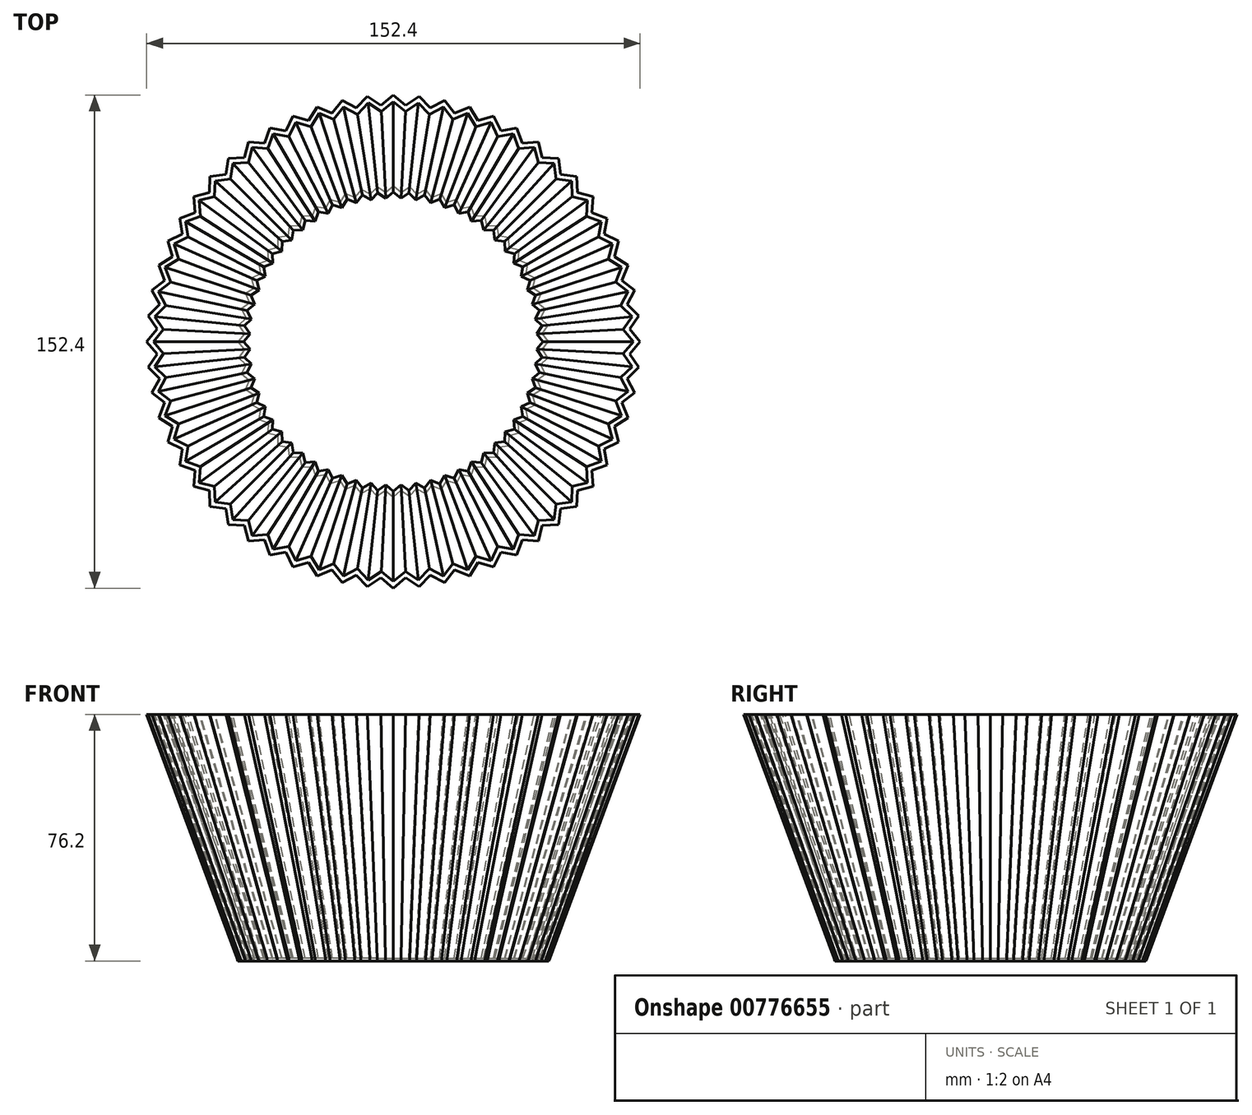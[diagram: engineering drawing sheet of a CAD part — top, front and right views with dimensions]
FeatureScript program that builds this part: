
annotation { "Feature Type Name" : "Feature", "Feature Type Description" : "" }
export const myFeature = defineFeature(function(context is Context, id is Id, definition is map)
    precondition{}
    {
        {
            var Q0;
            Q0=qCreatedBy(makeId("Top.planeOp"),FACE);
            var sketch = newSketch(context, id + "F0", { "sketchPlane" : qUnion([Q0])});
            skLineSegment(sketch, "E0", {"start": v(0, 0) * mm, "end": v(3.83, 73) * mm, "construction": true});
            skLineSegment(sketch, "E1", {"start": v(3.83, 73) * mm, "end": v(0, 73) * mm, "construction": true});
            skLineSegment(sketch, "E2", {"start": v(0, 73) * mm, "end": v(0, 0) * mm, "construction": true});
            skLineSegment(sketch, "E3", {"start": v(3.83, 73) * mm, "end": v(0, 76.2) * mm});
            skLineSegment(sketch, "E4.MirrorCS", {"start": v(-3.83, 73) * mm, "end": v(0, 76.2) * mm});
            skLineSegment(sketch, "E5.1.0", {"start": v(-11.43, 72.2) * mm, "end": v(-7.97, 75.78) * mm});
            skLineSegment(sketch, "E5.1.1", {"start": v(-3.83, 73) * mm, "end": v(-7.97, 75.78) * mm});
            skLineSegment(sketch, "E5.2.0", {"start": v(-18.92, 70.6) * mm, "end": v(-15.84, 74.53) * mm});
            skLineSegment(sketch, "E5.2.1", {"start": v(-11.43, 72.2) * mm, "end": v(-15.84, 74.53) * mm});
            skLineSegment(sketch, "E5.3.0", {"start": v(-26.2, 68.24) * mm, "end": v(-23.55, 72.47) * mm});
            skLineSegment(sketch, "E5.3.1", {"start": v(-18.92, 70.6) * mm, "end": v(-23.55, 72.47) * mm});
            skLineSegment(sketch, "E5.4.0", {"start": v(-33.18, 65.12) * mm, "end": v(-31, 69.61) * mm});
            skLineSegment(sketch, "E5.4.1", {"start": v(-26.2, 68.24) * mm, "end": v(-31, 69.61) * mm});
            skLineSegment(sketch, "E5.5.0", {"start": v(-39.8, 61.3) * mm, "end": v(-38.1, 66) * mm});
            skLineSegment(sketch, "E5.5.1", {"start": v(-33.18, 65.12) * mm, "end": v(-38.1, 66) * mm});
            skLineSegment(sketch, "E5.6.0", {"start": v(-46, 56.8) * mm, "end": v(-44.79, 61.65) * mm});
            skLineSegment(sketch, "E5.6.1", {"start": v(-39.8, 61.3) * mm, "end": v(-44.79, 61.65) * mm});
            skLineSegment(sketch, "E5.7.0", {"start": v(-51.68, 51.68) * mm, "end": v(-50.99, 56.63) * mm});
            skLineSegment(sketch, "E5.7.1", {"start": v(-46, 56.8) * mm, "end": v(-50.99, 56.63) * mm});
            skLineSegment(sketch, "E5.8.0", {"start": v(-56.8, 46) * mm, "end": v(-56.63, 50.99) * mm});
            skLineSegment(sketch, "E5.8.1", {"start": v(-51.68, 51.68) * mm, "end": v(-56.63, 50.99) * mm});
            skLineSegment(sketch, "E5.9.0", {"start": v(-61.3, 39.8) * mm, "end": v(-61.65, 44.79) * mm});
            skLineSegment(sketch, "E5.9.1", {"start": v(-56.8, 46) * mm, "end": v(-61.65, 44.79) * mm});
            skLineSegment(sketch, "E5.10.0", {"start": v(-65.12, 33.18) * mm, "end": v(-66, 38.1) * mm});
            skLineSegment(sketch, "E5.10.1", {"start": v(-61.3, 39.8) * mm, "end": v(-66, 38.1) * mm});
            skLineSegment(sketch, "E5.11.0", {"start": v(-68.24, 26.2) * mm, "end": v(-69.61, 31) * mm});
            skLineSegment(sketch, "E5.11.1", {"start": v(-65.12, 33.18) * mm, "end": v(-69.61, 31) * mm});
            skLineSegment(sketch, "E5.12.0", {"start": v(-70.6, 18.92) * mm, "end": v(-72.47, 23.55) * mm});
            skLineSegment(sketch, "E5.12.1", {"start": v(-68.24, 26.2) * mm, "end": v(-72.47, 23.55) * mm});
            skLineSegment(sketch, "E5.13.0", {"start": v(-72.2, 11.43) * mm, "end": v(-74.53, 15.84) * mm});
            skLineSegment(sketch, "E5.13.1", {"start": v(-70.6, 18.92) * mm, "end": v(-74.53, 15.84) * mm});
            skLineSegment(sketch, "E5.14.0", {"start": v(-73, 3.83) * mm, "end": v(-75.78, 7.97) * mm});
            skLineSegment(sketch, "E5.14.1", {"start": v(-72.2, 11.43) * mm, "end": v(-75.78, 7.97) * mm});
            skLineSegment(sketch, "E5.15.0", {"start": v(-73, -3.83) * mm, "end": v(-76.2, 0) * mm});
            skLineSegment(sketch, "E5.15.1", {"start": v(-73, 3.83) * mm, "end": v(-76.2, 0) * mm});
            skLineSegment(sketch, "E5.16.0", {"start": v(-72.2, -11.43) * mm, "end": v(-75.78, -7.97) * mm});
            skLineSegment(sketch, "E5.16.1", {"start": v(-73, -3.83) * mm, "end": v(-75.78, -7.97) * mm});
            skLineSegment(sketch, "E5.17.0", {"start": v(-70.6, -18.92) * mm, "end": v(-74.53, -15.84) * mm});
            skLineSegment(sketch, "E5.17.1", {"start": v(-72.2, -11.43) * mm, "end": v(-74.53, -15.84) * mm});
            skLineSegment(sketch, "E5.18.0", {"start": v(-68.24, -26.2) * mm, "end": v(-72.47, -23.55) * mm});
            skLineSegment(sketch, "E5.18.1", {"start": v(-70.6, -18.92) * mm, "end": v(-72.47, -23.55) * mm});
            skLineSegment(sketch, "E5.19.0", {"start": v(-65.12, -33.18) * mm, "end": v(-69.61, -31) * mm});
            skLineSegment(sketch, "E5.19.1", {"start": v(-68.24, -26.2) * mm, "end": v(-69.61, -31) * mm});
            skLineSegment(sketch, "E5.20.0", {"start": v(-61.3, -39.8) * mm, "end": v(-66, -38.1) * mm});
            skLineSegment(sketch, "E5.20.1", {"start": v(-65.12, -33.18) * mm, "end": v(-66, -38.1) * mm});
            skLineSegment(sketch, "E5.21.0", {"start": v(-56.8, -46) * mm, "end": v(-61.65, -44.79) * mm});
            skLineSegment(sketch, "E5.21.1", {"start": v(-61.3, -39.8) * mm, "end": v(-61.65, -44.79) * mm});
            skLineSegment(sketch, "E5.22.0", {"start": v(-51.68, -51.68) * mm, "end": v(-56.63, -50.99) * mm});
            skLineSegment(sketch, "E5.22.1", {"start": v(-56.8, -46) * mm, "end": v(-56.63, -50.99) * mm});
            skLineSegment(sketch, "E5.23.0", {"start": v(-46, -56.8) * mm, "end": v(-50.99, -56.63) * mm});
            skLineSegment(sketch, "E5.23.1", {"start": v(-51.68, -51.68) * mm, "end": v(-50.99, -56.63) * mm});
            skLineSegment(sketch, "E5.24.0", {"start": v(-39.8, -61.3) * mm, "end": v(-44.79, -61.65) * mm});
            skLineSegment(sketch, "E5.24.1", {"start": v(-46, -56.8) * mm, "end": v(-44.79, -61.65) * mm});
            skLineSegment(sketch, "E5.25.0", {"start": v(-33.18, -65.12) * mm, "end": v(-38.1, -66) * mm});
            skLineSegment(sketch, "E5.25.1", {"start": v(-39.8, -61.3) * mm, "end": v(-38.1, -66) * mm});
            skLineSegment(sketch, "E5.26.0", {"start": v(-26.2, -68.24) * mm, "end": v(-31, -69.61) * mm});
            skLineSegment(sketch, "E5.26.1", {"start": v(-33.18, -65.12) * mm, "end": v(-31, -69.61) * mm});
            skLineSegment(sketch, "E5.27.0", {"start": v(-18.92, -70.6) * mm, "end": v(-23.55, -72.47) * mm});
            skLineSegment(sketch, "E5.27.1", {"start": v(-26.2, -68.24) * mm, "end": v(-23.55, -72.47) * mm});
            skLineSegment(sketch, "E5.28.0", {"start": v(-11.43, -72.2) * mm, "end": v(-15.84, -74.53) * mm});
            skLineSegment(sketch, "E5.28.1", {"start": v(-18.92, -70.6) * mm, "end": v(-15.84, -74.53) * mm});
            skLineSegment(sketch, "E5.29.0", {"start": v(-3.83, -73) * mm, "end": v(-7.97, -75.78) * mm});
            skLineSegment(sketch, "E5.29.1", {"start": v(-11.43, -72.2) * mm, "end": v(-7.97, -75.78) * mm});
            skLineSegment(sketch, "E5.30.0", {"start": v(3.83, -73) * mm, "end": v(0, -76.2) * mm});
            skLineSegment(sketch, "E5.30.1", {"start": v(-3.83, -73) * mm, "end": v(0, -76.2) * mm});
            skLineSegment(sketch, "E5.31.0", {"start": v(11.43, -72.2) * mm, "end": v(7.97, -75.78) * mm});
            skLineSegment(sketch, "E5.31.1", {"start": v(3.83, -73) * mm, "end": v(7.97, -75.78) * mm});
            skLineSegment(sketch, "E5.32.0", {"start": v(18.92, -70.6) * mm, "end": v(15.84, -74.53) * mm});
            skLineSegment(sketch, "E5.32.1", {"start": v(11.43, -72.2) * mm, "end": v(15.84, -74.53) * mm});
            skLineSegment(sketch, "E5.33.0", {"start": v(26.2, -68.24) * mm, "end": v(23.55, -72.47) * mm});
            skLineSegment(sketch, "E5.33.1", {"start": v(18.92, -70.6) * mm, "end": v(23.55, -72.47) * mm});
            skLineSegment(sketch, "E5.34.0", {"start": v(33.18, -65.12) * mm, "end": v(31, -69.61) * mm});
            skLineSegment(sketch, "E5.34.1", {"start": v(26.2, -68.24) * mm, "end": v(31, -69.61) * mm});
            skLineSegment(sketch, "E5.35.0", {"start": v(39.8, -61.3) * mm, "end": v(38.1, -66) * mm});
            skLineSegment(sketch, "E5.35.1", {"start": v(33.18, -65.12) * mm, "end": v(38.1, -66) * mm});
            skLineSegment(sketch, "E5.36.0", {"start": v(46, -56.8) * mm, "end": v(44.79, -61.65) * mm});
            skLineSegment(sketch, "E5.36.1", {"start": v(39.8, -61.3) * mm, "end": v(44.79, -61.65) * mm});
            skLineSegment(sketch, "E5.37.0", {"start": v(51.68, -51.68) * mm, "end": v(50.99, -56.63) * mm});
            skLineSegment(sketch, "E5.37.1", {"start": v(46, -56.8) * mm, "end": v(50.99, -56.63) * mm});
            skLineSegment(sketch, "E5.38.0", {"start": v(56.8, -46) * mm, "end": v(56.63, -50.99) * mm});
            skLineSegment(sketch, "E5.38.1", {"start": v(51.68, -51.68) * mm, "end": v(56.63, -50.99) * mm});
            skLineSegment(sketch, "E5.39.0", {"start": v(61.3, -39.8) * mm, "end": v(61.65, -44.79) * mm});
            skLineSegment(sketch, "E5.39.1", {"start": v(56.8, -46) * mm, "end": v(61.65, -44.79) * mm});
            skLineSegment(sketch, "E5.40.0", {"start": v(65.12, -33.18) * mm, "end": v(66, -38.1) * mm});
            skLineSegment(sketch, "E5.40.1", {"start": v(61.3, -39.8) * mm, "end": v(66, -38.1) * mm});
            skLineSegment(sketch, "E5.41.0", {"start": v(68.24, -26.2) * mm, "end": v(69.61, -31) * mm});
            skLineSegment(sketch, "E5.41.1", {"start": v(65.12, -33.18) * mm, "end": v(69.61, -31) * mm});
            skLineSegment(sketch, "E5.42.0", {"start": v(70.6, -18.92) * mm, "end": v(72.47, -23.55) * mm});
            skLineSegment(sketch, "E5.42.1", {"start": v(68.24, -26.2) * mm, "end": v(72.47, -23.55) * mm});
            skLineSegment(sketch, "E5.43.0", {"start": v(72.2, -11.43) * mm, "end": v(74.53, -15.84) * mm});
            skLineSegment(sketch, "E5.43.1", {"start": v(70.6, -18.92) * mm, "end": v(74.53, -15.84) * mm});
            skLineSegment(sketch, "E5.44.0", {"start": v(73, -3.83) * mm, "end": v(75.78, -7.97) * mm});
            skLineSegment(sketch, "E5.44.1", {"start": v(72.2, -11.43) * mm, "end": v(75.78, -7.97) * mm});
            skLineSegment(sketch, "E5.45.0", {"start": v(73, 3.83) * mm, "end": v(76.2, 0) * mm});
            skLineSegment(sketch, "E5.45.1", {"start": v(73, -3.83) * mm, "end": v(76.2, 0) * mm});
            skLineSegment(sketch, "E5.46.0", {"start": v(72.2, 11.43) * mm, "end": v(75.78, 7.97) * mm});
            skLineSegment(sketch, "E5.46.1", {"start": v(73, 3.83) * mm, "end": v(75.78, 7.97) * mm});
            skLineSegment(sketch, "E5.47.0", {"start": v(70.6, 18.92) * mm, "end": v(74.53, 15.84) * mm});
            skLineSegment(sketch, "E5.47.1", {"start": v(72.2, 11.43) * mm, "end": v(74.53, 15.84) * mm});
            skLineSegment(sketch, "E5.48.0", {"start": v(68.24, 26.2) * mm, "end": v(72.47, 23.55) * mm});
            skLineSegment(sketch, "E5.48.1", {"start": v(70.6, 18.92) * mm, "end": v(72.47, 23.55) * mm});
            skLineSegment(sketch, "E5.49.0", {"start": v(65.12, 33.18) * mm, "end": v(69.61, 31) * mm});
            skLineSegment(sketch, "E5.49.1", {"start": v(68.24, 26.2) * mm, "end": v(69.61, 31) * mm});
            skLineSegment(sketch, "E5.50.0", {"start": v(61.3, 39.8) * mm, "end": v(66, 38.1) * mm});
            skLineSegment(sketch, "E5.50.1", {"start": v(65.12, 33.18) * mm, "end": v(66, 38.1) * mm});
            skLineSegment(sketch, "E5.51.0", {"start": v(56.8, 46) * mm, "end": v(61.65, 44.79) * mm});
            skLineSegment(sketch, "E5.51.1", {"start": v(61.3, 39.8) * mm, "end": v(61.65, 44.79) * mm});
            skLineSegment(sketch, "E5.52.0", {"start": v(51.68, 51.68) * mm, "end": v(56.63, 50.99) * mm});
            skLineSegment(sketch, "E5.52.1", {"start": v(56.8, 46) * mm, "end": v(56.63, 50.99) * mm});
            skLineSegment(sketch, "E5.53.0", {"start": v(46, 56.8) * mm, "end": v(50.99, 56.63) * mm});
            skLineSegment(sketch, "E5.53.1", {"start": v(51.68, 51.68) * mm, "end": v(50.99, 56.63) * mm});
            skLineSegment(sketch, "E5.54.0", {"start": v(39.8, 61.3) * mm, "end": v(44.79, 61.65) * mm});
            skLineSegment(sketch, "E5.54.1", {"start": v(46, 56.8) * mm, "end": v(44.79, 61.65) * mm});
            skLineSegment(sketch, "E5.55.0", {"start": v(33.18, 65.12) * mm, "end": v(38.1, 66) * mm});
            skLineSegment(sketch, "E5.55.1", {"start": v(39.8, 61.3) * mm, "end": v(38.1, 66) * mm});
            skLineSegment(sketch, "E5.56.0", {"start": v(26.2, 68.24) * mm, "end": v(31, 69.61) * mm});
            skLineSegment(sketch, "E5.56.1", {"start": v(33.18, 65.12) * mm, "end": v(31, 69.61) * mm});
            skLineSegment(sketch, "E5.57.0", {"start": v(18.92, 70.6) * mm, "end": v(23.55, 72.47) * mm});
            skLineSegment(sketch, "E5.57.1", {"start": v(26.2, 68.24) * mm, "end": v(23.55, 72.47) * mm});
            skLineSegment(sketch, "E5.58.0", {"start": v(11.43, 72.2) * mm, "end": v(15.84, 74.53) * mm});
            skLineSegment(sketch, "E5.58.1", {"start": v(18.92, 70.6) * mm, "end": v(15.84, 74.53) * mm});
            skLineSegment(sketch, "E5.59.0", {"start": v(3.83, 73) * mm, "end": v(7.97, 75.78) * mm});
            skLineSegment(sketch, "E5.59.1", {"start": v(11.43, 72.2) * mm, "end": v(7.97, 75.78) * mm});
            skPoint(sketch, "E5.center", {"position": v(0, 0) * mm});
            skLineSegment(sketch, "E6.0", {"start": v(-68.68, 18.4) * mm, "end": v(-70.5, 22.9) * mm});
            skLineSegment(sketch, "E6.1", {"start": v(-66.38, 25.48) * mm, "end": v(-70.5, 22.9) * mm});
            skLineSegment(sketch, "E6.2", {"start": v(-66.38, 25.48) * mm, "end": v(-67.72, 30.15) * mm});
            skLineSegment(sketch, "E6.3", {"start": v(-63.35, 32.28) * mm, "end": v(-67.72, 30.15) * mm});
            skLineSegment(sketch, "E6.4", {"start": v(-63.35, 32.28) * mm, "end": v(-64.2, 37.06) * mm});
            skLineSegment(sketch, "E6.5", {"start": v(-59.63, 38.73) * mm, "end": v(-64.2, 37.06) * mm});
            skLineSegment(sketch, "E6.6", {"start": v(-59.63, 38.73) * mm, "end": v(-59.97, 43.57) * mm});
            skLineSegment(sketch, "E6.7", {"start": v(-55.26, 44.75) * mm, "end": v(-59.97, 43.57) * mm});
            skLineSegment(sketch, "E6.8", {"start": v(-55.26, 44.75) * mm, "end": v(-55.09, 49.6) * mm});
            skLineSegment(sketch, "E6.9", {"start": v(-50.28, 50.28) * mm, "end": v(-55.09, 49.6) * mm});
            skLineSegment(sketch, "E6.10", {"start": v(-50.28, 50.28) * mm, "end": v(-49.6, 55.09) * mm});
            skLineSegment(sketch, "E6.11", {"start": v(-44.75, 55.26) * mm, "end": v(-49.6, 55.09) * mm});
            skLineSegment(sketch, "E6.12", {"start": v(-44.75, 55.26) * mm, "end": v(-43.57, 59.97) * mm});
            skLineSegment(sketch, "E6.13", {"start": v(-38.73, 59.63) * mm, "end": v(-43.57, 59.97) * mm});
            skLineSegment(sketch, "E6.14", {"start": v(-38.73, 59.63) * mm, "end": v(-37.06, 64.2) * mm});
            skLineSegment(sketch, "E6.15", {"start": v(-32.28, 63.35) * mm, "end": v(-37.06, 64.2) * mm});
            skLineSegment(sketch, "E6.16", {"start": v(-32.28, 63.35) * mm, "end": v(-30.15, 67.72) * mm});
            skLineSegment(sketch, "E6.17", {"start": v(-25.48, 66.38) * mm, "end": v(-30.15, 67.72) * mm});
            skLineSegment(sketch, "E6.18", {"start": v(-25.48, 66.38) * mm, "end": v(-22.9, 70.5) * mm});
            skLineSegment(sketch, "E6.19", {"start": v(-18.4, 68.68) * mm, "end": v(-22.9, 70.5) * mm});
            skLineSegment(sketch, "E6.20", {"start": v(-18.4, 68.68) * mm, "end": v(-15.41, 72.5) * mm});
            skLineSegment(sketch, "E6.21", {"start": v(-11.12, 70.23) * mm, "end": v(-15.41, 72.5) * mm});
            skLineSegment(sketch, "E6.22", {"start": v(-11.12, 70.23) * mm, "end": v(-7.75, 73.72) * mm});
            skLineSegment(sketch, "E6.23", {"start": v(38.73, -59.63) * mm, "end": v(43.57, -59.97) * mm});
            skLineSegment(sketch, "E6.24", {"start": v(38.73, -59.63) * mm, "end": v(37.06, -64.2) * mm});
            skLineSegment(sketch, "E6.25", {"start": v(32.28, -63.35) * mm, "end": v(37.06, -64.2) * mm});
            skLineSegment(sketch, "E6.26", {"start": v(32.28, -63.35) * mm, "end": v(30.15, -67.72) * mm});
            skLineSegment(sketch, "E6.27", {"start": v(25.48, -66.38) * mm, "end": v(30.15, -67.72) * mm});
            skLineSegment(sketch, "E6.28", {"start": v(25.48, -66.38) * mm, "end": v(22.9, -70.5) * mm});
            skLineSegment(sketch, "E6.29", {"start": v(18.4, -68.68) * mm, "end": v(22.9, -70.5) * mm});
            skLineSegment(sketch, "E6.30", {"start": v(18.4, -68.68) * mm, "end": v(15.41, -72.5) * mm});
            skLineSegment(sketch, "E6.31", {"start": v(11.12, -70.23) * mm, "end": v(15.41, -72.5) * mm});
            skLineSegment(sketch, "E6.32", {"start": v(11.12, -70.23) * mm, "end": v(7.75, -73.72) * mm});
            skLineSegment(sketch, "E6.33", {"start": v(3.72, -71) * mm, "end": v(7.75, -73.72) * mm});
            skLineSegment(sketch, "E6.34", {"start": v(3.72, -71) * mm, "end": v(0, -74.13) * mm});
            skLineSegment(sketch, "E6.35", {"start": v(-3.72, -71) * mm, "end": v(0, -74.13) * mm});
            skLineSegment(sketch, "E6.36", {"start": v(-3.72, -71) * mm, "end": v(-7.75, -73.72) * mm});
            skLineSegment(sketch, "E6.37", {"start": v(-11.12, -70.23) * mm, "end": v(-7.75, -73.72) * mm});
            skLineSegment(sketch, "E6.38", {"start": v(-11.12, -70.23) * mm, "end": v(-15.41, -72.5) * mm});
            skLineSegment(sketch, "E6.39", {"start": v(-18.4, -68.68) * mm, "end": v(-15.41, -72.5) * mm});
            skLineSegment(sketch, "E6.40", {"start": v(-18.4, -68.68) * mm, "end": v(-22.9, -70.5) * mm});
            skLineSegment(sketch, "E6.41", {"start": v(-25.48, -66.38) * mm, "end": v(-22.9, -70.5) * mm});
            skLineSegment(sketch, "E6.42", {"start": v(-25.48, -66.38) * mm, "end": v(-30.15, -67.72) * mm});
            skLineSegment(sketch, "E6.43", {"start": v(-32.28, -63.35) * mm, "end": v(-30.15, -67.72) * mm});
            skLineSegment(sketch, "E6.44", {"start": v(-32.28, -63.35) * mm, "end": v(-37.06, -64.2) * mm});
            skLineSegment(sketch, "E6.45", {"start": v(-38.73, -59.63) * mm, "end": v(-37.06, -64.2) * mm});
            skLineSegment(sketch, "E6.46", {"start": v(-38.73, -59.63) * mm, "end": v(-43.57, -59.97) * mm});
            skLineSegment(sketch, "E6.47", {"start": v(-68.68, -18.4) * mm, "end": v(-70.5, -22.9) * mm});
            skLineSegment(sketch, "E6.48", {"start": v(-68.68, -18.4) * mm, "end": v(-72.5, -15.41) * mm});
            skLineSegment(sketch, "E6.49", {"start": v(-70.23, -11.12) * mm, "end": v(-72.5, -15.41) * mm});
            skLineSegment(sketch, "E6.50", {"start": v(-70.23, -11.12) * mm, "end": v(-73.72, -7.75) * mm});
            skLineSegment(sketch, "E6.51", {"start": v(-71, -3.72) * mm, "end": v(-73.72, -7.75) * mm});
            skLineSegment(sketch, "E6.52", {"start": v(-71, -3.72) * mm, "end": v(-74.13, 0) * mm});
            skLineSegment(sketch, "E6.53", {"start": v(-70.23, 11.12) * mm, "end": v(-72.5, 15.41) * mm});
            skLineSegment(sketch, "E6.54", {"start": v(-70.23, 11.12) * mm, "end": v(-73.72, 7.75) * mm});
            skLineSegment(sketch, "E6.55", {"start": v(-71, 3.72) * mm, "end": v(-73.72, 7.75) * mm});
            skLineSegment(sketch, "E6.56", {"start": v(-71, 3.72) * mm, "end": v(-74.13, 0) * mm});
            skLineSegment(sketch, "E6.57", {"start": v(-66.38, -25.48) * mm, "end": v(-70.5, -22.9) * mm});
            skLineSegment(sketch, "E6.58", {"start": v(-66.38, -25.48) * mm, "end": v(-67.72, -30.15) * mm});
            skLineSegment(sketch, "E6.59", {"start": v(-63.35, -32.28) * mm, "end": v(-67.72, -30.15) * mm});
            skLineSegment(sketch, "E6.60", {"start": v(-63.35, -32.28) * mm, "end": v(-64.2, -37.06) * mm});
            skLineSegment(sketch, "E6.63", {"start": v(-55.26, -44.75) * mm, "end": v(-59.97, -43.57) * mm});
            skLineSegment(sketch, "E6.64", {"start": v(-55.26, -44.75) * mm, "end": v(-55.09, -49.6) * mm});
            skLineSegment(sketch, "E6.65", {"start": v(-50.28, -50.28) * mm, "end": v(-55.09, -49.6) * mm});
            skLineSegment(sketch, "E6.66", {"start": v(-50.28, -50.28) * mm, "end": v(-49.6, -55.09) * mm});
            skLineSegment(sketch, "E6.67", {"start": v(-44.75, -55.26) * mm, "end": v(-49.6, -55.09) * mm});
            skLineSegment(sketch, "E6.68", {"start": v(-44.75, -55.26) * mm, "end": v(-43.57, -59.97) * mm});
            skLineSegment(sketch, "E6.69", {"start": v(44.75, -55.26) * mm, "end": v(43.57, -59.97) * mm});
            skLineSegment(sketch, "E6.70", {"start": v(44.75, -55.26) * mm, "end": v(49.6, -55.09) * mm});
            skLineSegment(sketch, "E6.71", {"start": v(50.28, -50.28) * mm, "end": v(49.6, -55.09) * mm});
            skLineSegment(sketch, "E6.72", {"start": v(50.28, -50.28) * mm, "end": v(55.09, -49.6) * mm});
            skLineSegment(sketch, "E6.73", {"start": v(55.26, -44.75) * mm, "end": v(55.09, -49.6) * mm});
            skLineSegment(sketch, "E6.74", {"start": v(55.26, -44.75) * mm, "end": v(59.97, -43.57) * mm});
            skLineSegment(sketch, "E6.75", {"start": v(59.63, -38.73) * mm, "end": v(59.97, -43.57) * mm});
            skLineSegment(sketch, "E6.76", {"start": v(59.63, -38.73) * mm, "end": v(64.2, -37.06) * mm});
            skLineSegment(sketch, "E6.77", {"start": v(63.35, -32.28) * mm, "end": v(64.2, -37.06) * mm});
            skLineSegment(sketch, "E6.78", {"start": v(63.35, -32.28) * mm, "end": v(67.72, -30.15) * mm});
            skLineSegment(sketch, "E6.79", {"start": v(66.38, -25.48) * mm, "end": v(67.72, -30.15) * mm});
            skLineSegment(sketch, "E6.80", {"start": v(66.38, -25.48) * mm, "end": v(70.5, -22.9) * mm});
            skLineSegment(sketch, "E6.81", {"start": v(68.68, -18.4) * mm, "end": v(70.5, -22.9) * mm});
            skLineSegment(sketch, "E6.82", {"start": v(68.68, -18.4) * mm, "end": v(72.5, -15.41) * mm});
            skLineSegment(sketch, "E6.83", {"start": v(70.23, -11.12) * mm, "end": v(72.5, -15.41) * mm});
            skLineSegment(sketch, "E6.84", {"start": v(70.23, -11.12) * mm, "end": v(73.72, -7.75) * mm});
            skLineSegment(sketch, "E6.85", {"start": v(71, -3.72) * mm, "end": v(73.72, -7.75) * mm});
            skLineSegment(sketch, "E6.86", {"start": v(71, -3.72) * mm, "end": v(74.13, 0) * mm});
            skLineSegment(sketch, "E6.87", {"start": v(71, 3.72) * mm, "end": v(74.13, 0) * mm});
            skLineSegment(sketch, "E6.88", {"start": v(71, 3.72) * mm, "end": v(73.72, 7.75) * mm});
            skLineSegment(sketch, "E6.89", {"start": v(70.23, 11.12) * mm, "end": v(73.72, 7.75) * mm});
            skLineSegment(sketch, "E6.90", {"start": v(70.23, 11.12) * mm, "end": v(72.5, 15.41) * mm});
            skLineSegment(sketch, "E6.91", {"start": v(68.68, 18.4) * mm, "end": v(72.5, 15.41) * mm});
            skLineSegment(sketch, "E6.92", {"start": v(-68.68, 18.4) * mm, "end": v(-72.5, 15.41) * mm});
            skLineSegment(sketch, "E6.93", {"start": v(68.68, 18.4) * mm, "end": v(70.5, 22.9) * mm});
            skLineSegment(sketch, "E6.94", {"start": v(66.38, 25.48) * mm, "end": v(70.5, 22.9) * mm});
            skLineSegment(sketch, "E6.95", {"start": v(66.38, 25.48) * mm, "end": v(67.72, 30.15) * mm});
            skLineSegment(sketch, "E6.96", {"start": v(63.35, 32.28) * mm, "end": v(67.72, 30.15) * mm});
            skLineSegment(sketch, "E6.97", {"start": v(63.35, 32.28) * mm, "end": v(64.2, 37.06) * mm});
            skLineSegment(sketch, "E6.98", {"start": v(59.63, 38.73) * mm, "end": v(64.2, 37.06) * mm});
            skLineSegment(sketch, "E6.99", {"start": v(59.63, 38.73) * mm, "end": v(59.97, 43.57) * mm});
            skLineSegment(sketch, "E6.100", {"start": v(55.26, 44.75) * mm, "end": v(59.97, 43.57) * mm});
            skLineSegment(sketch, "E6.101", {"start": v(55.26, 44.75) * mm, "end": v(55.09, 49.6) * mm});
            skLineSegment(sketch, "E6.102", {"start": v(50.28, 50.28) * mm, "end": v(55.09, 49.6) * mm});
            skLineSegment(sketch, "E6.103", {"start": v(50.28, 50.28) * mm, "end": v(49.6, 55.09) * mm});
            skLineSegment(sketch, "E6.104", {"start": v(44.75, 55.26) * mm, "end": v(49.6, 55.09) * mm});
            skLineSegment(sketch, "E6.105", {"start": v(44.75, 55.26) * mm, "end": v(43.57, 59.97) * mm});
            skLineSegment(sketch, "E6.106", {"start": v(38.73, 59.63) * mm, "end": v(43.57, 59.97) * mm});
            skLineSegment(sketch, "E6.107", {"start": v(38.73, 59.63) * mm, "end": v(37.06, 64.2) * mm});
            skLineSegment(sketch, "E6.108", {"start": v(32.28, 63.35) * mm, "end": v(37.06, 64.2) * mm});
            skLineSegment(sketch, "E6.109", {"start": v(32.28, 63.35) * mm, "end": v(30.15, 67.72) * mm});
            skLineSegment(sketch, "E6.110", {"start": v(25.48, 66.38) * mm, "end": v(30.15, 67.72) * mm});
            skLineSegment(sketch, "E6.111", {"start": v(25.48, 66.38) * mm, "end": v(22.9, 70.5) * mm});
            skLineSegment(sketch, "E6.112", {"start": v(18.4, 68.68) * mm, "end": v(22.9, 70.5) * mm});
            skLineSegment(sketch, "E6.113", {"start": v(18.4, 68.68) * mm, "end": v(15.41, 72.5) * mm});
            skLineSegment(sketch, "E6.114", {"start": v(11.12, 70.23) * mm, "end": v(15.41, 72.5) * mm});
            skLineSegment(sketch, "E6.115", {"start": v(11.12, 70.23) * mm, "end": v(7.75, 73.72) * mm});
            skLineSegment(sketch, "E6.116", {"start": v(3.72, 71) * mm, "end": v(7.75, 73.72) * mm});
            skLineSegment(sketch, "E6.117", {"start": v(3.72, 71) * mm, "end": v(0, 74.13) * mm});
            skLineSegment(sketch, "E6.118", {"start": v(-3.72, 71) * mm, "end": v(0, 74.13) * mm});
            skLineSegment(sketch, "E6.119", {"start": v(-3.72, 71) * mm, "end": v(-7.75, 73.72) * mm});
            skSolve(sketch);
        }
        {
            var Q0;
            Q0=qCreatedBy(makeId("Top.planeOp"),FACE);
            cPlane(context, id + "F1", {"entities" : qUnion([Q0]), "cplaneType" : CPlaneType.OFFSET, "offset" : 76.2 * mm, "oppositeDirection" : true, "width" : 152.4 * mm, "height" : 152.4 * mm});
        }
        {
            var Q0;
            Q0=qCreatedBy(id+"F1.planeOp",FACE);
            var sketch = newSketch(context, id + "F2", { "sketchPlane" : qUnion([Q0])});
            skLineSegment(sketch, "E7", {"start": v(0, 0) * mm, "end": v(0, 45.98) * mm, "construction": true});
            skLineSegment(sketch, "E8", {"start": v(0, 45.98) * mm, "end": v(2.4, 45.98) * mm, "construction": true});
            skLineSegment(sketch, "E9", {"start": v(2.4, 45.98) * mm, "end": v(0, 0) * mm, "construction": true});
            skLineSegment(sketch, "E10", {"start": v(2.4, 45.98) * mm, "end": v(0, 48) * mm});
            skLineSegment(sketch, "E11.MirrorCS", {"start": v(-2.4, 45.98) * mm, "end": v(0, 48) * mm});
            skLineSegment(sketch, "E12.1.0", {"start": v(-2.4, 45.98) * mm, "end": v(-5.02, 47.74) * mm});
            skLineSegment(sketch, "E12.1.1", {"start": v(-7.2, 45.48) * mm, "end": v(-5.02, 47.74) * mm});
            skLineSegment(sketch, "E12.2.0", {"start": v(-7.2, 45.48) * mm, "end": v(-9.98, 46.96) * mm});
            skLineSegment(sketch, "E12.2.1", {"start": v(-11.92, 44.48) * mm, "end": v(-9.98, 46.96) * mm});
            skLineSegment(sketch, "E12.3.0", {"start": v(-11.92, 44.48) * mm, "end": v(-14.83, 45.66) * mm});
            skLineSegment(sketch, "E12.3.1", {"start": v(-16.5, 42.99) * mm, "end": v(-14.83, 45.66) * mm});
            skLineSegment(sketch, "E12.4.0", {"start": v(-16.5, 42.99) * mm, "end": v(-19.53, 43.86) * mm});
            skLineSegment(sketch, "E12.4.1", {"start": v(-20.9, 41.03) * mm, "end": v(-19.53, 43.86) * mm});
            skLineSegment(sketch, "E12.5.0", {"start": v(-20.9, 41.03) * mm, "end": v(-24, 41.57) * mm});
            skLineSegment(sketch, "E12.5.1", {"start": v(-25.08, 38.62) * mm, "end": v(-24, 41.57) * mm});
            skLineSegment(sketch, "E12.6.0", {"start": v(-25.08, 38.62) * mm, "end": v(-28.22, 38.84) * mm});
            skLineSegment(sketch, "E12.6.1", {"start": v(-28.98, 35.79) * mm, "end": v(-28.22, 38.84) * mm});
            skLineSegment(sketch, "E12.7.0", {"start": v(-28.98, 35.79) * mm, "end": v(-32.12, 35.68) * mm});
            skLineSegment(sketch, "E12.7.1", {"start": v(-32.56, 32.56) * mm, "end": v(-32.12, 35.68) * mm});
            skLineSegment(sketch, "E12.8.0", {"start": v(-32.56, 32.56) * mm, "end": v(-35.68, 32.12) * mm});
            skLineSegment(sketch, "E12.8.1", {"start": v(-35.79, 28.98) * mm, "end": v(-35.68, 32.12) * mm});
            skLineSegment(sketch, "E12.9.0", {"start": v(-35.79, 28.98) * mm, "end": v(-38.84, 28.22) * mm});
            skLineSegment(sketch, "E12.9.1", {"start": v(-38.62, 25.08) * mm, "end": v(-38.84, 28.22) * mm});
            skLineSegment(sketch, "E12.10.0", {"start": v(-38.62, 25.08) * mm, "end": v(-41.57, 24) * mm});
            skLineSegment(sketch, "E12.10.1", {"start": v(-41.03, 20.9) * mm, "end": v(-41.57, 24) * mm});
            skLineSegment(sketch, "E12.11.0", {"start": v(-41.03, 20.9) * mm, "end": v(-43.86, 19.53) * mm});
            skLineSegment(sketch, "E12.11.1", {"start": v(-42.99, 16.5) * mm, "end": v(-43.86, 19.53) * mm});
            skLineSegment(sketch, "E12.12.0", {"start": v(-42.99, 16.5) * mm, "end": v(-45.66, 14.83) * mm});
            skLineSegment(sketch, "E12.12.1", {"start": v(-44.48, 11.92) * mm, "end": v(-45.66, 14.83) * mm});
            skLineSegment(sketch, "E12.13.0", {"start": v(-44.48, 11.92) * mm, "end": v(-46.96, 9.98) * mm});
            skLineSegment(sketch, "E12.13.1", {"start": v(-45.48, 7.2) * mm, "end": v(-46.96, 9.98) * mm});
            skLineSegment(sketch, "E12.14.0", {"start": v(-45.48, 7.2) * mm, "end": v(-47.74, 5.02) * mm});
            skLineSegment(sketch, "E12.14.1", {"start": v(-45.98, 2.4) * mm, "end": v(-47.74, 5.02) * mm});
            skLineSegment(sketch, "E12.15.0", {"start": v(-45.98, 2.4) * mm, "end": v(-48, 0) * mm});
            skLineSegment(sketch, "E12.15.1", {"start": v(-45.98, -2.4) * mm, "end": v(-48, 0) * mm});
            skLineSegment(sketch, "E12.16.0", {"start": v(-45.98, -2.4) * mm, "end": v(-47.74, -5.02) * mm});
            skLineSegment(sketch, "E12.16.1", {"start": v(-45.48, -7.2) * mm, "end": v(-47.74, -5.02) * mm});
            skLineSegment(sketch, "E12.17.0", {"start": v(-45.48, -7.2) * mm, "end": v(-46.96, -9.98) * mm});
            skLineSegment(sketch, "E12.17.1", {"start": v(-44.48, -11.92) * mm, "end": v(-46.96, -9.98) * mm});
            skLineSegment(sketch, "E12.18.0", {"start": v(-44.48, -11.92) * mm, "end": v(-45.66, -14.83) * mm});
            skLineSegment(sketch, "E12.18.1", {"start": v(-42.99, -16.5) * mm, "end": v(-45.66, -14.83) * mm});
            skLineSegment(sketch, "E12.19.0", {"start": v(-42.99, -16.5) * mm, "end": v(-43.86, -19.53) * mm});
            skLineSegment(sketch, "E12.19.1", {"start": v(-41.03, -20.9) * mm, "end": v(-43.86, -19.53) * mm});
            skLineSegment(sketch, "E12.20.0", {"start": v(-41.03, -20.9) * mm, "end": v(-41.57, -24) * mm});
            skLineSegment(sketch, "E12.20.1", {"start": v(-38.62, -25.08) * mm, "end": v(-41.57, -24) * mm});
            skLineSegment(sketch, "E12.21.0", {"start": v(-38.62, -25.08) * mm, "end": v(-38.84, -28.22) * mm});
            skLineSegment(sketch, "E12.21.1", {"start": v(-35.79, -28.98) * mm, "end": v(-38.84, -28.22) * mm});
            skLineSegment(sketch, "E12.22.0", {"start": v(-35.79, -28.98) * mm, "end": v(-35.68, -32.12) * mm});
            skLineSegment(sketch, "E12.22.1", {"start": v(-32.56, -32.56) * mm, "end": v(-35.68, -32.12) * mm});
            skLineSegment(sketch, "E12.23.0", {"start": v(-32.56, -32.56) * mm, "end": v(-32.12, -35.68) * mm});
            skLineSegment(sketch, "E12.23.1", {"start": v(-28.98, -35.79) * mm, "end": v(-32.12, -35.68) * mm});
            skLineSegment(sketch, "E12.24.0", {"start": v(-28.98, -35.79) * mm, "end": v(-28.22, -38.84) * mm});
            skLineSegment(sketch, "E12.24.1", {"start": v(-25.08, -38.62) * mm, "end": v(-28.22, -38.84) * mm});
            skLineSegment(sketch, "E12.25.0", {"start": v(-25.08, -38.62) * mm, "end": v(-24, -41.57) * mm});
            skLineSegment(sketch, "E12.25.1", {"start": v(-20.9, -41.03) * mm, "end": v(-24, -41.57) * mm});
            skLineSegment(sketch, "E12.26.0", {"start": v(-20.9, -41.03) * mm, "end": v(-19.53, -43.86) * mm});
            skLineSegment(sketch, "E12.26.1", {"start": v(-16.5, -42.99) * mm, "end": v(-19.53, -43.86) * mm});
            skLineSegment(sketch, "E12.27.0", {"start": v(-16.5, -42.99) * mm, "end": v(-14.83, -45.66) * mm});
            skLineSegment(sketch, "E12.27.1", {"start": v(-11.92, -44.48) * mm, "end": v(-14.83, -45.66) * mm});
            skLineSegment(sketch, "E12.28.0", {"start": v(-11.92, -44.48) * mm, "end": v(-9.98, -46.96) * mm});
            skLineSegment(sketch, "E12.28.1", {"start": v(-7.2, -45.48) * mm, "end": v(-9.98, -46.96) * mm});
            skLineSegment(sketch, "E12.29.0", {"start": v(-7.2, -45.48) * mm, "end": v(-5.02, -47.74) * mm});
            skLineSegment(sketch, "E12.29.1", {"start": v(-2.4, -45.98) * mm, "end": v(-5.02, -47.74) * mm});
            skLineSegment(sketch, "E12.30.0", {"start": v(-2.4, -45.98) * mm, "end": v(0, -48) * mm});
            skLineSegment(sketch, "E12.30.1", {"start": v(2.4, -45.98) * mm, "end": v(0, -48) * mm});
            skLineSegment(sketch, "E12.31.0", {"start": v(2.4, -45.98) * mm, "end": v(5.02, -47.74) * mm});
            skLineSegment(sketch, "E12.31.1", {"start": v(7.2, -45.48) * mm, "end": v(5.02, -47.74) * mm});
            skLineSegment(sketch, "E12.32.0", {"start": v(7.2, -45.48) * mm, "end": v(9.98, -46.96) * mm});
            skLineSegment(sketch, "E12.32.1", {"start": v(11.92, -44.48) * mm, "end": v(9.98, -46.96) * mm});
            skLineSegment(sketch, "E12.33.0", {"start": v(11.92, -44.48) * mm, "end": v(14.83, -45.66) * mm});
            skLineSegment(sketch, "E12.33.1", {"start": v(16.5, -42.99) * mm, "end": v(14.83, -45.66) * mm});
            skLineSegment(sketch, "E12.34.0", {"start": v(16.5, -42.99) * mm, "end": v(19.53, -43.86) * mm});
            skLineSegment(sketch, "E12.34.1", {"start": v(20.9, -41.03) * mm, "end": v(19.53, -43.86) * mm});
            skLineSegment(sketch, "E12.35.0", {"start": v(20.9, -41.03) * mm, "end": v(24, -41.57) * mm});
            skLineSegment(sketch, "E12.35.1", {"start": v(25.08, -38.62) * mm, "end": v(24, -41.57) * mm});
            skLineSegment(sketch, "E12.36.0", {"start": v(25.08, -38.62) * mm, "end": v(28.22, -38.84) * mm});
            skLineSegment(sketch, "E12.36.1", {"start": v(28.98, -35.79) * mm, "end": v(28.22, -38.84) * mm});
            skLineSegment(sketch, "E12.37.0", {"start": v(28.98, -35.79) * mm, "end": v(32.12, -35.68) * mm});
            skLineSegment(sketch, "E12.37.1", {"start": v(32.56, -32.56) * mm, "end": v(32.12, -35.68) * mm});
            skLineSegment(sketch, "E12.38.0", {"start": v(32.56, -32.56) * mm, "end": v(35.68, -32.12) * mm});
            skLineSegment(sketch, "E12.38.1", {"start": v(35.79, -28.98) * mm, "end": v(35.68, -32.12) * mm});
            skLineSegment(sketch, "E12.39.0", {"start": v(35.79, -28.98) * mm, "end": v(38.84, -28.22) * mm});
            skLineSegment(sketch, "E12.39.1", {"start": v(38.62, -25.08) * mm, "end": v(38.84, -28.22) * mm});
            skLineSegment(sketch, "E12.40.0", {"start": v(38.62, -25.08) * mm, "end": v(41.57, -24) * mm});
            skLineSegment(sketch, "E12.40.1", {"start": v(41.03, -20.9) * mm, "end": v(41.57, -24) * mm});
            skLineSegment(sketch, "E12.41.0", {"start": v(41.03, -20.9) * mm, "end": v(43.86, -19.53) * mm});
            skLineSegment(sketch, "E12.41.1", {"start": v(42.99, -16.5) * mm, "end": v(43.86, -19.53) * mm});
            skLineSegment(sketch, "E12.42.0", {"start": v(42.99, -16.5) * mm, "end": v(45.66, -14.83) * mm});
            skLineSegment(sketch, "E12.42.1", {"start": v(44.48, -11.92) * mm, "end": v(45.66, -14.83) * mm});
            skLineSegment(sketch, "E12.43.0", {"start": v(44.48, -11.92) * mm, "end": v(46.96, -9.98) * mm});
            skLineSegment(sketch, "E12.43.1", {"start": v(45.48, -7.2) * mm, "end": v(46.96, -9.98) * mm});
            skLineSegment(sketch, "E12.44.0", {"start": v(45.48, -7.2) * mm, "end": v(47.74, -5.02) * mm});
            skLineSegment(sketch, "E12.44.1", {"start": v(45.98, -2.4) * mm, "end": v(47.74, -5.02) * mm});
            skLineSegment(sketch, "E12.45.0", {"start": v(45.98, -2.4) * mm, "end": v(48, 0) * mm});
            skLineSegment(sketch, "E12.45.1", {"start": v(45.98, 2.4) * mm, "end": v(48, 0) * mm});
            skLineSegment(sketch, "E12.46.0", {"start": v(45.98, 2.4) * mm, "end": v(47.74, 5.02) * mm});
            skLineSegment(sketch, "E12.46.1", {"start": v(45.48, 7.2) * mm, "end": v(47.74, 5.02) * mm});
            skLineSegment(sketch, "E12.47.0", {"start": v(45.48, 7.2) * mm, "end": v(46.96, 9.98) * mm});
            skLineSegment(sketch, "E12.47.1", {"start": v(44.48, 11.92) * mm, "end": v(46.96, 9.98) * mm});
            skLineSegment(sketch, "E12.48.0", {"start": v(44.48, 11.92) * mm, "end": v(45.66, 14.83) * mm});
            skLineSegment(sketch, "E12.48.1", {"start": v(42.99, 16.5) * mm, "end": v(45.66, 14.83) * mm});
            skLineSegment(sketch, "E12.49.0", {"start": v(42.99, 16.5) * mm, "end": v(43.86, 19.53) * mm});
            skLineSegment(sketch, "E12.49.1", {"start": v(41.03, 20.9) * mm, "end": v(43.86, 19.53) * mm});
            skLineSegment(sketch, "E12.50.0", {"start": v(41.03, 20.9) * mm, "end": v(41.57, 24) * mm});
            skLineSegment(sketch, "E12.50.1", {"start": v(38.62, 25.08) * mm, "end": v(41.57, 24) * mm});
            skLineSegment(sketch, "E12.51.0", {"start": v(38.62, 25.08) * mm, "end": v(38.84, 28.22) * mm});
            skLineSegment(sketch, "E12.51.1", {"start": v(35.79, 28.98) * mm, "end": v(38.84, 28.22) * mm});
            skLineSegment(sketch, "E12.52.0", {"start": v(35.79, 28.98) * mm, "end": v(35.68, 32.12) * mm});
            skLineSegment(sketch, "E12.52.1", {"start": v(32.56, 32.56) * mm, "end": v(35.68, 32.12) * mm});
            skLineSegment(sketch, "E12.53.0", {"start": v(32.56, 32.56) * mm, "end": v(32.12, 35.68) * mm});
            skLineSegment(sketch, "E12.53.1", {"start": v(28.98, 35.79) * mm, "end": v(32.12, 35.68) * mm});
            skLineSegment(sketch, "E12.54.0", {"start": v(28.98, 35.79) * mm, "end": v(28.22, 38.84) * mm});
            skLineSegment(sketch, "E12.54.1", {"start": v(25.08, 38.62) * mm, "end": v(28.22, 38.84) * mm});
            skLineSegment(sketch, "E12.55.0", {"start": v(25.08, 38.62) * mm, "end": v(24, 41.57) * mm});
            skLineSegment(sketch, "E12.55.1", {"start": v(20.9, 41.03) * mm, "end": v(24, 41.57) * mm});
            skLineSegment(sketch, "E12.56.0", {"start": v(20.9, 41.03) * mm, "end": v(19.53, 43.86) * mm});
            skLineSegment(sketch, "E12.56.1", {"start": v(16.5, 42.99) * mm, "end": v(19.53, 43.86) * mm});
            skLineSegment(sketch, "E12.57.0", {"start": v(16.5, 42.99) * mm, "end": v(14.83, 45.66) * mm});
            skLineSegment(sketch, "E12.57.1", {"start": v(11.92, 44.48) * mm, "end": v(14.83, 45.66) * mm});
            skLineSegment(sketch, "E12.58.0", {"start": v(11.92, 44.48) * mm, "end": v(9.98, 46.96) * mm});
            skLineSegment(sketch, "E12.58.1", {"start": v(7.2, 45.48) * mm, "end": v(9.98, 46.96) * mm});
            skLineSegment(sketch, "E12.59.0", {"start": v(7.2, 45.48) * mm, "end": v(5.02, 47.74) * mm});
            skLineSegment(sketch, "E12.59.1", {"start": v(2.4, 45.98) * mm, "end": v(5.02, 47.74) * mm});
            skPoint(sketch, "E12.center", {"position": v(0, 0) * mm});
            skLineSegment(sketch, "E13.0", {"start": v(-15.79, 41.13) * mm, "end": v(-18.68, 41.96) * mm});
            skLineSegment(sketch, "E13.1", {"start": v(-20, 39.26) * mm, "end": v(-18.68, 41.96) * mm});
            skLineSegment(sketch, "E13.2", {"start": v(-20, 39.26) * mm, "end": v(-22.97, 39.78) * mm});
            skLineSegment(sketch, "E13.3", {"start": v(-24, 36.95) * mm, "end": v(-22.97, 39.78) * mm});
            skLineSegment(sketch, "E13.4", {"start": v(-24, 36.95) * mm, "end": v(-27, 37.16) * mm});
            skLineSegment(sketch, "E13.5", {"start": v(-27.73, 34.24) * mm, "end": v(-27, 37.16) * mm});
            skLineSegment(sketch, "E13.6", {"start": v(-27.73, 34.24) * mm, "end": v(-30.74, 34.14) * mm});
            skLineSegment(sketch, "E13.7", {"start": v(-31.15, 31.15) * mm, "end": v(-30.74, 34.14) * mm});
            skLineSegment(sketch, "E13.8", {"start": v(-31.15, 31.15) * mm, "end": v(-34.14, 30.74) * mm});
            skLineSegment(sketch, "E13.9", {"start": v(-34.24, 27.73) * mm, "end": v(-34.14, 30.74) * mm});
            skLineSegment(sketch, "E13.10", {"start": v(-34.24, 27.73) * mm, "end": v(-37.16, 27) * mm});
            skLineSegment(sketch, "E13.11", {"start": v(-36.95, 24) * mm, "end": v(-37.16, 27) * mm});
            skLineSegment(sketch, "E13.13", {"start": v(-39.26, 20) * mm, "end": v(-39.78, 22.97) * mm});
            skLineSegment(sketch, "E13.14", {"start": v(-39.26, 20) * mm, "end": v(-41.96, 18.68) * mm});
            skLineSegment(sketch, "E13.15", {"start": v(-41.13, 15.79) * mm, "end": v(-41.96, 18.68) * mm});
            skLineSegment(sketch, "E13.16", {"start": v(-41.13, 15.79) * mm, "end": v(-43.69, 14.2) * mm});
            skLineSegment(sketch, "E13.17", {"start": v(-42.56, 11.4) * mm, "end": v(-43.69, 14.2) * mm});
            skLineSegment(sketch, "E13.18", {"start": v(-42.56, 11.4) * mm, "end": v(-44.93, 9.55) * mm});
            skLineSegment(sketch, "E13.19", {"start": v(-43.52, 6.9) * mm, "end": v(-44.93, 9.55) * mm});
            skLineSegment(sketch, "E13.20", {"start": v(-43.52, 6.9) * mm, "end": v(-45.68, 4.8) * mm});
            skLineSegment(sketch, "E13.21", {"start": v(-44, 2.3) * mm, "end": v(-45.68, 4.8) * mm});
            skLineSegment(sketch, "E13.22", {"start": v(-44, 2.3) * mm, "end": v(-45.93, 0) * mm});
            skLineSegment(sketch, "E13.23", {"start": v(39.26, -20) * mm, "end": v(39.78, -22.97) * mm});
            skLineSegment(sketch, "E13.24", {"start": v(39.26, -20) * mm, "end": v(41.96, -18.68) * mm});
            skLineSegment(sketch, "E13.25", {"start": v(41.13, -15.79) * mm, "end": v(41.96, -18.68) * mm});
            skLineSegment(sketch, "E13.26", {"start": v(41.13, -15.79) * mm, "end": v(43.69, -14.2) * mm});
            skLineSegment(sketch, "E13.27", {"start": v(42.56, -11.4) * mm, "end": v(43.69, -14.2) * mm});
            skLineSegment(sketch, "E13.28", {"start": v(42.56, -11.4) * mm, "end": v(44.93, -9.55) * mm});
            skLineSegment(sketch, "E13.29", {"start": v(43.52, -6.9) * mm, "end": v(44.93, -9.55) * mm});
            skLineSegment(sketch, "E13.30", {"start": v(43.52, -6.9) * mm, "end": v(45.68, -4.8) * mm});
            skLineSegment(sketch, "E13.31", {"start": v(44, -2.3) * mm, "end": v(45.68, -4.8) * mm});
            skLineSegment(sketch, "E13.32", {"start": v(44, -2.3) * mm, "end": v(45.93, 0) * mm});
            skLineSegment(sketch, "E13.33", {"start": v(44, 2.3) * mm, "end": v(45.93, 0) * mm});
            skLineSegment(sketch, "E13.35", {"start": v(43.52, 6.9) * mm, "end": v(45.68, 4.8) * mm});
            skLineSegment(sketch, "E13.36", {"start": v(43.52, 6.9) * mm, "end": v(44.93, 9.55) * mm});
            skLineSegment(sketch, "E13.37", {"start": v(42.56, 11.4) * mm, "end": v(44.93, 9.55) * mm});
            skLineSegment(sketch, "E13.38", {"start": v(42.56, 11.4) * mm, "end": v(43.69, 14.2) * mm});
            skLineSegment(sketch, "E13.39", {"start": v(41.13, 15.79) * mm, "end": v(43.69, 14.2) * mm});
            skLineSegment(sketch, "E13.40", {"start": v(41.13, 15.79) * mm, "end": v(41.96, 18.68) * mm});
            skLineSegment(sketch, "E13.41", {"start": v(39.26, 20) * mm, "end": v(41.96, 18.68) * mm});
            skLineSegment(sketch, "E13.42", {"start": v(39.26, 20) * mm, "end": v(39.78, 22.97) * mm});
            skLineSegment(sketch, "E13.43", {"start": v(36.95, 24) * mm, "end": v(39.78, 22.97) * mm});
            skLineSegment(sketch, "E13.44", {"start": v(36.95, 24) * mm, "end": v(37.16, 27) * mm});
            skLineSegment(sketch, "E13.45", {"start": v(34.24, 27.73) * mm, "end": v(37.16, 27) * mm});
            skLineSegment(sketch, "E13.46", {"start": v(34.24, 27.73) * mm, "end": v(34.14, 30.74) * mm});
            skLineSegment(sketch, "E13.47", {"start": v(6.9, 43.52) * mm, "end": v(9.55, 44.93) * mm});
            skLineSegment(sketch, "E13.48", {"start": v(6.9, 43.52) * mm, "end": v(4.8, 45.68) * mm});
            skLineSegment(sketch, "E13.49", {"start": v(2.3, 44) * mm, "end": v(4.8, 45.68) * mm});
            skLineSegment(sketch, "E13.50", {"start": v(2.3, 44) * mm, "end": v(0, 45.93) * mm});
            skLineSegment(sketch, "E13.51", {"start": v(-2.3, 44) * mm, "end": v(0, 45.93) * mm});
            skLineSegment(sketch, "E13.52", {"start": v(-2.3, 44) * mm, "end": v(-4.8, 45.68) * mm});
            skLineSegment(sketch, "E13.53", {"start": v(-11.4, 42.56) * mm, "end": v(-14.2, 43.69) * mm});
            skLineSegment(sketch, "E13.54", {"start": v(-11.4, 42.56) * mm, "end": v(-9.55, 44.93) * mm});
            skLineSegment(sketch, "E13.55", {"start": v(-6.9, 43.52) * mm, "end": v(-9.55, 44.93) * mm});
            skLineSegment(sketch, "E13.56", {"start": v(-6.9, 43.52) * mm, "end": v(-4.8, 45.68) * mm});
            skLineSegment(sketch, "E13.57", {"start": v(11.4, 42.56) * mm, "end": v(9.55, 44.93) * mm});
            skLineSegment(sketch, "E13.58", {"start": v(11.4, 42.56) * mm, "end": v(14.2, 43.69) * mm});
            skLineSegment(sketch, "E13.59", {"start": v(15.79, 41.13) * mm, "end": v(14.2, 43.69) * mm});
            skLineSegment(sketch, "E13.60", {"start": v(15.79, 41.13) * mm, "end": v(18.68, 41.96) * mm});
            skLineSegment(sketch, "E13.61", {"start": v(20, 39.26) * mm, "end": v(18.68, 41.96) * mm});
            skLineSegment(sketch, "E13.62", {"start": v(20, 39.26) * mm, "end": v(22.97, 39.78) * mm});
            skLineSegment(sketch, "E13.63", {"start": v(24, 36.95) * mm, "end": v(22.97, 39.78) * mm});
            skLineSegment(sketch, "E13.64", {"start": v(24, 36.95) * mm, "end": v(27, 37.16) * mm});
            skLineSegment(sketch, "E13.65", {"start": v(27.73, 34.24) * mm, "end": v(27, 37.16) * mm});
            skLineSegment(sketch, "E13.66", {"start": v(27.73, 34.24) * mm, "end": v(30.74, 34.14) * mm});
            skLineSegment(sketch, "E13.67", {"start": v(31.15, 31.15) * mm, "end": v(30.74, 34.14) * mm});
            skLineSegment(sketch, "E13.68", {"start": v(31.15, 31.15) * mm, "end": v(34.14, 30.74) * mm});
            skLineSegment(sketch, "E13.69", {"start": v(36.95, -24) * mm, "end": v(39.78, -22.97) * mm});
            skLineSegment(sketch, "E13.70", {"start": v(36.95, -24) * mm, "end": v(37.16, -27) * mm});
            skLineSegment(sketch, "E13.71", {"start": v(34.24, -27.73) * mm, "end": v(37.16, -27) * mm});
            skLineSegment(sketch, "E13.72", {"start": v(34.24, -27.73) * mm, "end": v(34.14, -30.74) * mm});
            skLineSegment(sketch, "E13.73", {"start": v(31.15, -31.15) * mm, "end": v(34.14, -30.74) * mm});
            skLineSegment(sketch, "E13.74", {"start": v(31.15, -31.15) * mm, "end": v(30.74, -34.14) * mm});
            skLineSegment(sketch, "E13.75", {"start": v(27.73, -34.24) * mm, "end": v(30.74, -34.14) * mm});
            skLineSegment(sketch, "E13.76", {"start": v(27.73, -34.24) * mm, "end": v(27, -37.16) * mm});
            skLineSegment(sketch, "E13.77", {"start": v(24, -36.95) * mm, "end": v(27, -37.16) * mm});
            skLineSegment(sketch, "E13.78", {"start": v(24, -36.95) * mm, "end": v(22.97, -39.78) * mm});
            skLineSegment(sketch, "E13.79", {"start": v(20, -39.26) * mm, "end": v(22.97, -39.78) * mm});
            skLineSegment(sketch, "E13.80", {"start": v(20, -39.26) * mm, "end": v(18.68, -41.96) * mm});
            skLineSegment(sketch, "E13.81", {"start": v(15.79, -41.13) * mm, "end": v(18.68, -41.96) * mm});
            skLineSegment(sketch, "E13.82", {"start": v(15.79, -41.13) * mm, "end": v(14.2, -43.69) * mm});
            skLineSegment(sketch, "E13.83", {"start": v(11.4, -42.56) * mm, "end": v(14.2, -43.69) * mm});
            skLineSegment(sketch, "E13.84", {"start": v(11.4, -42.56) * mm, "end": v(9.55, -44.93) * mm});
            skLineSegment(sketch, "E13.85", {"start": v(6.9, -43.52) * mm, "end": v(9.55, -44.93) * mm});
            skLineSegment(sketch, "E13.86", {"start": v(6.9, -43.52) * mm, "end": v(4.8, -45.68) * mm});
            skLineSegment(sketch, "E13.87", {"start": v(2.3, -44) * mm, "end": v(4.8, -45.68) * mm});
            skLineSegment(sketch, "E13.88", {"start": v(2.3, -44) * mm, "end": v(0, -45.93) * mm});
            skLineSegment(sketch, "E13.89", {"start": v(-2.3, -44) * mm, "end": v(0, -45.93) * mm});
            skLineSegment(sketch, "E13.90", {"start": v(-2.3, -44) * mm, "end": v(-4.8, -45.68) * mm});
            skLineSegment(sketch, "E13.91", {"start": v(-6.9, -43.52) * mm, "end": v(-4.8, -45.68) * mm});
            skLineSegment(sketch, "E13.92", {"start": v(-15.79, 41.13) * mm, "end": v(-14.2, 43.69) * mm});
            skLineSegment(sketch, "E13.93", {"start": v(-6.9, -43.52) * mm, "end": v(-9.55, -44.93) * mm});
            skLineSegment(sketch, "E13.94", {"start": v(-11.4, -42.56) * mm, "end": v(-9.55, -44.93) * mm});
            skLineSegment(sketch, "E13.95", {"start": v(-11.4, -42.56) * mm, "end": v(-14.2, -43.69) * mm});
            skLineSegment(sketch, "E13.96", {"start": v(-15.79, -41.13) * mm, "end": v(-14.2, -43.69) * mm});
            skLineSegment(sketch, "E13.97", {"start": v(-15.79, -41.13) * mm, "end": v(-18.68, -41.96) * mm});
            skLineSegment(sketch, "E13.98", {"start": v(-20, -39.26) * mm, "end": v(-18.68, -41.96) * mm});
            skLineSegment(sketch, "E13.99", {"start": v(-20, -39.26) * mm, "end": v(-22.97, -39.78) * mm});
            skLineSegment(sketch, "E13.100", {"start": v(-24, -36.95) * mm, "end": v(-22.97, -39.78) * mm});
            skLineSegment(sketch, "E13.101", {"start": v(-24, -36.95) * mm, "end": v(-27, -37.16) * mm});
            skLineSegment(sketch, "E13.102", {"start": v(-27.73, -34.24) * mm, "end": v(-27, -37.16) * mm});
            skLineSegment(sketch, "E13.103", {"start": v(-27.73, -34.24) * mm, "end": v(-30.74, -34.14) * mm});
            skLineSegment(sketch, "E13.104", {"start": v(-31.15, -31.15) * mm, "end": v(-30.74, -34.14) * mm});
            skLineSegment(sketch, "E13.105", {"start": v(-31.15, -31.15) * mm, "end": v(-34.14, -30.74) * mm});
            skLineSegment(sketch, "E13.106", {"start": v(-34.24, -27.73) * mm, "end": v(-34.14, -30.74) * mm});
            skLineSegment(sketch, "E13.107", {"start": v(-34.24, -27.73) * mm, "end": v(-37.16, -27) * mm});
            skLineSegment(sketch, "E13.108", {"start": v(-36.95, -24) * mm, "end": v(-37.16, -27) * mm});
            skLineSegment(sketch, "E13.109", {"start": v(-36.95, -24) * mm, "end": v(-39.78, -22.97) * mm});
            skLineSegment(sketch, "E13.110", {"start": v(-39.26, -20) * mm, "end": v(-39.78, -22.97) * mm});
            skLineSegment(sketch, "E13.111", {"start": v(-39.26, -20) * mm, "end": v(-41.96, -18.68) * mm});
            skLineSegment(sketch, "E13.112", {"start": v(-41.13, -15.79) * mm, "end": v(-41.96, -18.68) * mm});
            skLineSegment(sketch, "E13.113", {"start": v(-41.13, -15.79) * mm, "end": v(-43.69, -14.2) * mm});
            skLineSegment(sketch, "E13.114", {"start": v(-42.56, -11.4) * mm, "end": v(-43.69, -14.2) * mm});
            skLineSegment(sketch, "E13.115", {"start": v(-42.56, -11.4) * mm, "end": v(-44.93, -9.55) * mm});
            skLineSegment(sketch, "E13.116", {"start": v(-43.52, -6.9) * mm, "end": v(-44.93, -9.55) * mm});
            skLineSegment(sketch, "E13.117", {"start": v(-43.52, -6.9) * mm, "end": v(-45.68, -4.8) * mm});
            skLineSegment(sketch, "E13.118", {"start": v(-44, -2.3) * mm, "end": v(-45.68, -4.8) * mm});
            skLineSegment(sketch, "E13.119", {"start": v(-44, -2.3) * mm, "end": v(-45.93, 0) * mm});
            skSolve(sketch);
        }
        {
            var Q0;
            Q0=makeQuery(id+"F0.imprint","IMPRINT",FACE,{"disambiguationData":[TD([[makeQuery(id+"F0.imprint","IMPRINT",EDGE,{"derivedFrom":sQuery(id+"F0.wireOp",EDGE,"E3")}),1.0]])]});
            var Q1;
            Q1=makeQuery(id+"F2.imprint","IMPRINT",FACE,{"disambiguationData":[TD([[makeQuery(id+"F2.imprint","IMPRINT",EDGE,{"derivedFrom":sQuery(id+"F2.wireOp",EDGE,"E10")}),1.0]])]});
            loft(context, id + "F3", {"sheetProfilesArray" : [{ "sheetProfileEntities" : qUnion([Q0]) }, { "sheetProfileEntities" : qUnion([Q1]) }]});
        }
        {
            var Q0;
            Q0=qCreatedBy(id+"F1.planeOp",FACE);
            cPlane(context, id + "F4", {"entities" : qUnion([Q0]), "cplaneType" : CPlaneType.OFFSET, "offset" : 0.8 * mm, "width" : 152.4 * mm, "height" : 152.4 * mm});
        }
        {
            var Q0;
            Q0=qCreatedBy(id+"F4.planeOp",FACE);
            var sketch = newSketch(context, id + "F5", { "sketchPlane" : qUnion([Q0])});
            skLineSegment(sketch, "E14.bottom", {"start": v(-57.12, -67.57) * mm, "end": v(57.14, -67.57) * mm});
            skLineSegment(sketch, "E14.top", {"start": v(-57.12, 55.66) * mm, "end": v(57.14, 55.66) * mm});
            skLineSegment(sketch, "E14.left", {"start": v(-57.12, -67.57) * mm, "end": v(-57.12, 55.66) * mm});
            skLineSegment(sketch, "E14.right", {"start": v(57.14, -67.57) * mm, "end": v(57.14, 55.66) * mm});
            skSolve(sketch);
        }
        {
            var Q0;
            Q0 = qSketchRegion(id + "F5", true);
            extrude(context, id + "F6", {"entities" : qUnion([Q0]), "operationType" : NewBodyOperationType.REMOVE, "oppositeDirection" : true, "depth" : 25.4 * mm, "offsetDistance" : 25.4 * mm});
        }
        {
            var Q0;
            Q0=makeQuery(id+"F6.boolean.opBoolean","COPY",FACE,{"derivedFrom":makeQuery(id+"F6.opExtrude","CAP_FACE",FACE,{"disambiguationData":[OSD([sQuery(id+"F5.wireOp",EDGE,"E14.bottom"),sQuery(id+"F5.wireOp",EDGE,"E14.top"),sQuery(id+"F5.wireOp",EDGE,"E14.left"),sQuery(id+"F5.wireOp",EDGE,"E14.right")])],"isStart":true})});
            var sketch = newSketch(context, id + "F7", { "sketchPlane" : qUnion([Q0])});
            skLineSegment(sketch, "E15.0", {"start": v(-4.83, 45.97) * mm, "end": v(-6.94, 43.8) * mm});
            skLineSegment(sketch, "E15.1", {"start": v(-2.32, 44.28) * mm, "end": v(-4.83, 45.97) * mm});
            skLineSegment(sketch, "E15.2", {"start": v(0, 46.23) * mm, "end": v(-2.32, 44.28) * mm});
            skLineSegment(sketch, "E15.3", {"start": v(2.32, 44.28) * mm, "end": v(0, 46.23) * mm});
            skLineSegment(sketch, "E15.4", {"start": v(4.83, 45.97) * mm, "end": v(2.32, 44.28) * mm});
            skLineSegment(sketch, "E15.5", {"start": v(6.94, 43.8) * mm, "end": v(4.83, 45.97) * mm});
            skLineSegment(sketch, "E15.6", {"start": v(9.61, 45.22) * mm, "end": v(6.94, 43.8) * mm});
            skLineSegment(sketch, "E15.7", {"start": v(11.48, 42.83) * mm, "end": v(9.61, 45.22) * mm});
            skLineSegment(sketch, "E15.8", {"start": v(14.29, 43.96) * mm, "end": v(11.48, 42.83) * mm});
            skLineSegment(sketch, "E15.9", {"start": v(15.9, 41.4) * mm, "end": v(14.29, 43.96) * mm});
            skLineSegment(sketch, "E15.10", {"start": v(18.8, 42.23) * mm, "end": v(15.9, 41.4) * mm});
            skLineSegment(sketch, "E15.11", {"start": v(20.13, 39.5) * mm, "end": v(18.8, 42.23) * mm});
            skLineSegment(sketch, "E15.12", {"start": v(23.11, 40.03) * mm, "end": v(20.13, 39.5) * mm});
            skLineSegment(sketch, "E15.13", {"start": v(24.15, 37.19) * mm, "end": v(23.11, 40.03) * mm});
            skLineSegment(sketch, "E15.14", {"start": v(27.17, 37.4) * mm, "end": v(24.15, 37.19) * mm});
            skLineSegment(sketch, "E15.15", {"start": v(27.9, 34.46) * mm, "end": v(27.17, 37.4) * mm});
            skLineSegment(sketch, "E15.16", {"start": v(30.93, 34.35) * mm, "end": v(27.9, 34.46) * mm});
            skLineSegment(sketch, "E15.17", {"start": v(31.35, 31.35) * mm, "end": v(30.93, 34.35) * mm});
            skLineSegment(sketch, "E15.18", {"start": v(34.35, 30.93) * mm, "end": v(31.35, 31.35) * mm});
            skLineSegment(sketch, "E15.19", {"start": v(34.46, 27.9) * mm, "end": v(34.35, 30.93) * mm});
            skLineSegment(sketch, "E15.20", {"start": v(37.4, 27.17) * mm, "end": v(34.46, 27.9) * mm});
            skLineSegment(sketch, "E15.21", {"start": v(37.19, 24.15) * mm, "end": v(37.4, 27.17) * mm});
            skLineSegment(sketch, "E15.22", {"start": v(40.03, 23.11) * mm, "end": v(37.19, 24.15) * mm});
            skLineSegment(sketch, "E15.23", {"start": v(-24.15, -37.19) * mm, "end": v(-23.11, -40.03) * mm});
            skLineSegment(sketch, "E15.24", {"start": v(-27.17, -37.4) * mm, "end": v(-24.15, -37.19) * mm});
            skLineSegment(sketch, "E15.25", {"start": v(-27.9, -34.46) * mm, "end": v(-27.17, -37.4) * mm});
            skLineSegment(sketch, "E15.26", {"start": v(-30.93, -34.35) * mm, "end": v(-27.9, -34.46) * mm});
            skLineSegment(sketch, "E15.27", {"start": v(-31.35, -31.35) * mm, "end": v(-30.93, -34.35) * mm});
            skLineSegment(sketch, "E15.28", {"start": v(-34.35, -30.93) * mm, "end": v(-31.35, -31.35) * mm});
            skLineSegment(sketch, "E15.29", {"start": v(-34.46, -27.9) * mm, "end": v(-34.35, -30.93) * mm});
            skLineSegment(sketch, "E15.30", {"start": v(-37.4, -27.17) * mm, "end": v(-34.46, -27.9) * mm});
            skLineSegment(sketch, "E15.31", {"start": v(-37.19, -24.15) * mm, "end": v(-37.4, -27.17) * mm});
            skLineSegment(sketch, "E15.32", {"start": v(-40.03, -23.11) * mm, "end": v(-37.19, -24.15) * mm});
            skLineSegment(sketch, "E15.33", {"start": v(-39.5, -20.13) * mm, "end": v(-40.03, -23.11) * mm});
            skLineSegment(sketch, "E15.34", {"start": v(-42.23, -18.8) * mm, "end": v(-39.5, -20.13) * mm});
            skLineSegment(sketch, "E15.35", {"start": v(-41.4, -15.9) * mm, "end": v(-42.23, -18.8) * mm});
            skLineSegment(sketch, "E15.36", {"start": v(-43.96, -14.29) * mm, "end": v(-41.4, -15.9) * mm});
            skLineSegment(sketch, "E15.37", {"start": v(-42.83, -11.48) * mm, "end": v(-43.96, -14.29) * mm});
            skLineSegment(sketch, "E15.38", {"start": v(-45.22, -9.61) * mm, "end": v(-42.83, -11.48) * mm});
            skLineSegment(sketch, "E15.39", {"start": v(-43.8, -6.94) * mm, "end": v(-45.22, -9.61) * mm});
            skLineSegment(sketch, "E15.40", {"start": v(-45.97, -4.83) * mm, "end": v(-43.8, -6.94) * mm});
            skLineSegment(sketch, "E15.41", {"start": v(-44.28, -2.32) * mm, "end": v(-45.97, -4.83) * mm});
            skLineSegment(sketch, "E15.42", {"start": v(-46.23, 0) * mm, "end": v(-44.28, -2.32) * mm});
            skLineSegment(sketch, "E15.43", {"start": v(-44.28, 2.32) * mm, "end": v(-46.23, 0) * mm});
            skLineSegment(sketch, "E15.44", {"start": v(-45.97, 4.83) * mm, "end": v(-44.28, 2.32) * mm});
            skLineSegment(sketch, "E15.45", {"start": v(-43.8, 6.94) * mm, "end": v(-45.97, 4.83) * mm});
            skLineSegment(sketch, "E15.46", {"start": v(-45.22, 9.61) * mm, "end": v(-43.8, 6.94) * mm});
            skLineSegment(sketch, "E15.47", {"start": v(-27.9, 34.46) * mm, "end": v(-30.93, 34.35) * mm});
            skLineSegment(sketch, "E15.48", {"start": v(-27.17, 37.4) * mm, "end": v(-27.9, 34.46) * mm});
            skLineSegment(sketch, "E15.49", {"start": v(-24.15, 37.19) * mm, "end": v(-27.17, 37.4) * mm});
            skLineSegment(sketch, "E15.50", {"start": v(-23.11, 40.03) * mm, "end": v(-24.15, 37.19) * mm});
            skLineSegment(sketch, "E15.51", {"start": v(-20.13, 39.5) * mm, "end": v(-23.11, 40.03) * mm});
            skLineSegment(sketch, "E15.52", {"start": v(-18.8, 42.23) * mm, "end": v(-20.13, 39.5) * mm});
            skLineSegment(sketch, "E15.53", {"start": v(-9.61, 45.22) * mm, "end": v(-11.48, 42.83) * mm});
            skLineSegment(sketch, "E15.54", {"start": v(-11.48, 42.83) * mm, "end": v(-14.29, 43.96) * mm});
            skLineSegment(sketch, "E15.55", {"start": v(-14.29, 43.96) * mm, "end": v(-15.9, 41.4) * mm});
            skLineSegment(sketch, "E15.56", {"start": v(-15.9, 41.4) * mm, "end": v(-18.8, 42.23) * mm});
            skLineSegment(sketch, "E15.57", {"start": v(-30.93, 34.35) * mm, "end": v(-31.35, 31.35) * mm});
            skLineSegment(sketch, "E15.58", {"start": v(-31.35, 31.35) * mm, "end": v(-34.35, 30.93) * mm});
            skLineSegment(sketch, "E15.59", {"start": v(-34.35, 30.93) * mm, "end": v(-34.46, 27.9) * mm});
            skLineSegment(sketch, "E15.60", {"start": v(-34.46, 27.9) * mm, "end": v(-37.4, 27.17) * mm});
            skLineSegment(sketch, "E15.61", {"start": v(-37.4, 27.17) * mm, "end": v(-37.19, 24.15) * mm});
            skLineSegment(sketch, "E15.62", {"start": v(-37.19, 24.15) * mm, "end": v(-40.03, 23.11) * mm});
            skLineSegment(sketch, "E15.63", {"start": v(-40.03, 23.11) * mm, "end": v(-39.5, 20.13) * mm});
            skLineSegment(sketch, "E15.64", {"start": v(-39.5, 20.13) * mm, "end": v(-42.23, 18.8) * mm});
            skLineSegment(sketch, "E15.65", {"start": v(-42.23, 18.8) * mm, "end": v(-41.4, 15.9) * mm});
            skLineSegment(sketch, "E15.66", {"start": v(-41.4, 15.9) * mm, "end": v(-43.96, 14.29) * mm});
            skLineSegment(sketch, "E15.67", {"start": v(-43.96, 14.29) * mm, "end": v(-42.83, 11.48) * mm});
            skLineSegment(sketch, "E15.68", {"start": v(-42.83, 11.48) * mm, "end": v(-45.22, 9.61) * mm});
            skLineSegment(sketch, "E15.69", {"start": v(-23.11, -40.03) * mm, "end": v(-20.13, -39.5) * mm});
            skLineSegment(sketch, "E15.70", {"start": v(-20.13, -39.5) * mm, "end": v(-18.8, -42.23) * mm});
            skLineSegment(sketch, "E15.71", {"start": v(-18.8, -42.23) * mm, "end": v(-15.9, -41.4) * mm});
            skLineSegment(sketch, "E15.72", {"start": v(-15.9, -41.4) * mm, "end": v(-14.29, -43.96) * mm});
            skLineSegment(sketch, "E15.73", {"start": v(-14.29, -43.96) * mm, "end": v(-11.48, -42.83) * mm});
            skLineSegment(sketch, "E15.74", {"start": v(-11.48, -42.83) * mm, "end": v(-9.61, -45.22) * mm});
            skLineSegment(sketch, "E15.75", {"start": v(-9.61, -45.22) * mm, "end": v(-6.94, -43.8) * mm});
            skLineSegment(sketch, "E15.76", {"start": v(-6.94, -43.8) * mm, "end": v(-4.83, -45.97) * mm});
            skLineSegment(sketch, "E15.77", {"start": v(-4.83, -45.97) * mm, "end": v(-2.32, -44.28) * mm});
            skLineSegment(sketch, "E15.78", {"start": v(-2.32, -44.28) * mm, "end": v(0, -46.23) * mm});
            skLineSegment(sketch, "E15.79", {"start": v(0, -46.23) * mm, "end": v(2.32, -44.28) * mm});
            skLineSegment(sketch, "E15.80", {"start": v(2.32, -44.28) * mm, "end": v(4.83, -45.97) * mm});
            skLineSegment(sketch, "E15.81", {"start": v(4.83, -45.97) * mm, "end": v(6.94, -43.8) * mm});
            skLineSegment(sketch, "E15.82", {"start": v(6.94, -43.8) * mm, "end": v(9.61, -45.22) * mm});
            skLineSegment(sketch, "E15.83", {"start": v(9.61, -45.22) * mm, "end": v(11.48, -42.83) * mm});
            skLineSegment(sketch, "E15.84", {"start": v(11.48, -42.83) * mm, "end": v(14.29, -43.96) * mm});
            skLineSegment(sketch, "E15.85", {"start": v(14.29, -43.96) * mm, "end": v(15.9, -41.4) * mm});
            skLineSegment(sketch, "E15.86", {"start": v(15.9, -41.4) * mm, "end": v(18.8, -42.23) * mm});
            skLineSegment(sketch, "E15.87", {"start": v(18.8, -42.23) * mm, "end": v(20.13, -39.5) * mm});
            skLineSegment(sketch, "E15.88", {"start": v(20.13, -39.5) * mm, "end": v(23.11, -40.03) * mm});
            skLineSegment(sketch, "E15.89", {"start": v(23.11, -40.03) * mm, "end": v(24.15, -37.19) * mm});
            skLineSegment(sketch, "E15.90", {"start": v(24.15, -37.19) * mm, "end": v(27.17, -37.4) * mm});
            skLineSegment(sketch, "E15.91", {"start": v(27.17, -37.4) * mm, "end": v(27.9, -34.46) * mm});
            skLineSegment(sketch, "E15.92", {"start": v(-6.94, 43.8) * mm, "end": v(-9.61, 45.22) * mm});
            skLineSegment(sketch, "E15.93", {"start": v(27.9, -34.46) * mm, "end": v(30.93, -34.35) * mm});
            skLineSegment(sketch, "E15.94", {"start": v(30.93, -34.35) * mm, "end": v(31.35, -31.35) * mm});
            skLineSegment(sketch, "E15.95", {"start": v(31.35, -31.35) * mm, "end": v(34.35, -30.93) * mm});
            skLineSegment(sketch, "E15.96", {"start": v(34.35, -30.93) * mm, "end": v(34.46, -27.9) * mm});
            skLineSegment(sketch, "E15.97", {"start": v(34.46, -27.9) * mm, "end": v(37.4, -27.17) * mm});
            skLineSegment(sketch, "E15.98", {"start": v(37.4, -27.17) * mm, "end": v(37.19, -24.15) * mm});
            skLineSegment(sketch, "E15.99", {"start": v(37.19, -24.15) * mm, "end": v(40.03, -23.11) * mm});
            skLineSegment(sketch, "E15.100", {"start": v(40.03, -23.11) * mm, "end": v(39.5, -20.13) * mm});
            skLineSegment(sketch, "E15.101", {"start": v(39.5, -20.13) * mm, "end": v(42.23, -18.8) * mm});
            skLineSegment(sketch, "E15.102", {"start": v(42.23, -18.8) * mm, "end": v(41.4, -15.9) * mm});
            skLineSegment(sketch, "E15.103", {"start": v(41.4, -15.9) * mm, "end": v(43.96, -14.29) * mm});
            skLineSegment(sketch, "E15.104", {"start": v(43.96, -14.29) * mm, "end": v(42.83, -11.48) * mm});
            skLineSegment(sketch, "E15.105", {"start": v(42.83, -11.48) * mm, "end": v(45.22, -9.61) * mm});
            skLineSegment(sketch, "E15.106", {"start": v(45.22, -9.61) * mm, "end": v(43.8, -6.94) * mm});
            skLineSegment(sketch, "E15.107", {"start": v(43.8, -6.94) * mm, "end": v(45.97, -4.83) * mm});
            skLineSegment(sketch, "E15.108", {"start": v(45.97, -4.83) * mm, "end": v(44.28, -2.32) * mm});
            skLineSegment(sketch, "E15.109", {"start": v(44.28, -2.32) * mm, "end": v(46.23, 0) * mm});
            skLineSegment(sketch, "E15.110", {"start": v(46.23, 0) * mm, "end": v(44.28, 2.32) * mm});
            skLineSegment(sketch, "E15.111", {"start": v(44.28, 2.32) * mm, "end": v(45.97, 4.83) * mm});
            skLineSegment(sketch, "E15.112", {"start": v(45.97, 4.83) * mm, "end": v(43.8, 6.94) * mm});
            skLineSegment(sketch, "E15.113", {"start": v(43.8, 6.94) * mm, "end": v(45.22, 9.61) * mm});
            skLineSegment(sketch, "E15.114", {"start": v(45.22, 9.61) * mm, "end": v(42.83, 11.48) * mm});
            skLineSegment(sketch, "E15.115", {"start": v(42.83, 11.48) * mm, "end": v(43.96, 14.29) * mm});
            skLineSegment(sketch, "E15.116", {"start": v(43.96, 14.29) * mm, "end": v(41.4, 15.9) * mm});
            skLineSegment(sketch, "E15.117", {"start": v(41.4, 15.9) * mm, "end": v(42.23, 18.8) * mm});
            skLineSegment(sketch, "E15.118", {"start": v(42.23, 18.8) * mm, "end": v(39.5, 20.13) * mm});
            skLineSegment(sketch, "E15.119", {"start": v(39.5, 20.13) * mm, "end": v(40.03, 23.11) * mm});
            skSolve(sketch);
        }
        {
            var Q0;
            Q0=makeQuery(id+"F0.imprint","IMPRINT",FACE,{"disambiguationData":[TD([[makeQuery(id+"F0.imprint","IMPRINT",EDGE,{"derivedFrom":sQuery(id+"F0.wireOp",EDGE,"E3")}),1.0]])]});
            var sketch = newSketch(context, id + "F8", { "sketchPlane" : qUnion([Q0])});
            skLineSegment(sketch, "E16.0.0", {"start": v(-7.97, -75.78) * mm, "end": v(-3.83, -73) * mm, "construction": true});
            skLineSegment(sketch, "E16.0.1", {"start": v(-3.83, -73) * mm, "end": v(0, -76.2) * mm, "construction": true});
            skLineSegment(sketch, "E16.0.2", {"start": v(0, -76.2) * mm, "end": v(3.83, -73) * mm, "construction": true});
            skLineSegment(sketch, "E16.0.3", {"start": v(3.83, -73) * mm, "end": v(7.97, -75.78) * mm, "construction": true});
            skLineSegment(sketch, "E16.0.4", {"start": v(7.97, -75.78) * mm, "end": v(11.43, -72.2) * mm, "construction": true});
            skLineSegment(sketch, "E16.0.5", {"start": v(11.43, -72.2) * mm, "end": v(15.84, -74.53) * mm, "construction": true});
            skLineSegment(sketch, "E16.0.6", {"start": v(15.84, -74.53) * mm, "end": v(18.92, -70.6) * mm, "construction": true});
            skLineSegment(sketch, "E16.0.7", {"start": v(18.92, -70.6) * mm, "end": v(23.55, -72.47) * mm, "construction": true});
            skLineSegment(sketch, "E16.0.8", {"start": v(23.55, -72.47) * mm, "end": v(26.2, -68.24) * mm, "construction": true});
            skLineSegment(sketch, "E16.0.9", {"start": v(26.2, -68.24) * mm, "end": v(31, -69.61) * mm, "construction": true});
            skLineSegment(sketch, "E16.0.10", {"start": v(31, -69.61) * mm, "end": v(33.18, -65.12) * mm, "construction": true});
            skLineSegment(sketch, "E16.0.11", {"start": v(33.18, -65.12) * mm, "end": v(38.1, -66) * mm, "construction": true});
            skLineSegment(sketch, "E16.0.12", {"start": v(38.1, -66) * mm, "end": v(39.8, -61.3) * mm, "construction": true});
            skLineSegment(sketch, "E16.0.13", {"start": v(39.8, -61.3) * mm, "end": v(44.79, -61.65) * mm, "construction": true});
            skLineSegment(sketch, "E16.0.14", {"start": v(44.79, -61.65) * mm, "end": v(46, -56.8) * mm, "construction": true});
            skLineSegment(sketch, "E16.0.15", {"start": v(46, -56.8) * mm, "end": v(50.99, -56.63) * mm, "construction": true});
            skLineSegment(sketch, "E16.0.16", {"start": v(50.99, -56.63) * mm, "end": v(51.68, -51.68) * mm, "construction": true});
            skLineSegment(sketch, "E16.0.17", {"start": v(51.68, -51.68) * mm, "end": v(56.63, -50.99) * mm, "construction": true});
            skLineSegment(sketch, "E16.0.18", {"start": v(56.63, -50.99) * mm, "end": v(56.8, -46) * mm, "construction": true});
            skLineSegment(sketch, "E16.0.19", {"start": v(56.8, -46) * mm, "end": v(61.65, -44.79) * mm, "construction": true});
            skLineSegment(sketch, "E16.0.20", {"start": v(61.65, -44.79) * mm, "end": v(61.3, -39.8) * mm, "construction": true});
            skLineSegment(sketch, "E16.0.21", {"start": v(61.3, -39.8) * mm, "end": v(66, -38.1) * mm, "construction": true});
            skLineSegment(sketch, "E16.0.22", {"start": v(66, -38.1) * mm, "end": v(65.12, -33.18) * mm, "construction": true});
            skLineSegment(sketch, "E16.0.23", {"start": v(65.12, -33.18) * mm, "end": v(69.61, -31) * mm, "construction": true});
            skLineSegment(sketch, "E16.0.24", {"start": v(69.61, -31) * mm, "end": v(68.24, -26.2) * mm, "construction": true});
            skLineSegment(sketch, "E16.0.25", {"start": v(68.24, -26.2) * mm, "end": v(72.47, -23.55) * mm, "construction": true});
            skLineSegment(sketch, "E16.0.26", {"start": v(72.47, -23.55) * mm, "end": v(70.6, -18.92) * mm, "construction": true});
            skLineSegment(sketch, "E16.0.27", {"start": v(70.6, -18.92) * mm, "end": v(74.53, -15.84) * mm, "construction": true});
            skLineSegment(sketch, "E16.0.28", {"start": v(74.53, -15.84) * mm, "end": v(72.2, -11.43) * mm, "construction": true});
            skLineSegment(sketch, "E16.0.29", {"start": v(72.2, -11.43) * mm, "end": v(75.78, -7.97) * mm, "construction": true});
            skLineSegment(sketch, "E16.0.30", {"start": v(75.78, -7.97) * mm, "end": v(73, -3.83) * mm, "construction": true});
            skLineSegment(sketch, "E16.0.31", {"start": v(73, -3.83) * mm, "end": v(76.2, 0) * mm, "construction": true});
            skLineSegment(sketch, "E16.0.32", {"start": v(76.2, 0) * mm, "end": v(73, 3.83) * mm, "construction": true});
            skLineSegment(sketch, "E16.0.33", {"start": v(73, 3.83) * mm, "end": v(75.78, 7.97) * mm, "construction": true});
            skLineSegment(sketch, "E16.0.34", {"start": v(75.78, 7.97) * mm, "end": v(72.2, 11.43) * mm, "construction": true});
            skLineSegment(sketch, "E16.0.35", {"start": v(72.2, 11.43) * mm, "end": v(74.53, 15.84) * mm, "construction": true});
            skLineSegment(sketch, "E16.0.36", {"start": v(74.53, 15.84) * mm, "end": v(70.6, 18.92) * mm, "construction": true});
            skLineSegment(sketch, "E16.0.37", {"start": v(70.6, 18.92) * mm, "end": v(72.47, 23.55) * mm, "construction": true});
            skLineSegment(sketch, "E16.0.38", {"start": v(72.47, 23.55) * mm, "end": v(68.24, 26.2) * mm, "construction": true});
            skLineSegment(sketch, "E16.0.39", {"start": v(68.24, 26.2) * mm, "end": v(69.61, 31) * mm, "construction": true});
            skLineSegment(sketch, "E16.0.40", {"start": v(69.61, 31) * mm, "end": v(65.12, 33.18) * mm, "construction": true});
            skLineSegment(sketch, "E16.0.41", {"start": v(65.12, 33.18) * mm, "end": v(66, 38.1) * mm, "construction": true});
            skLineSegment(sketch, "E16.0.42", {"start": v(66, 38.1) * mm, "end": v(61.3, 39.8) * mm, "construction": true});
            skLineSegment(sketch, "E16.0.43", {"start": v(61.3, 39.8) * mm, "end": v(61.65, 44.79) * mm, "construction": true});
            skLineSegment(sketch, "E16.0.44", {"start": v(61.65, 44.79) * mm, "end": v(56.8, 46) * mm, "construction": true});
            skLineSegment(sketch, "E16.0.45", {"start": v(56.8, 46) * mm, "end": v(56.63, 50.99) * mm, "construction": true});
            skLineSegment(sketch, "E16.0.46", {"start": v(56.63, 50.99) * mm, "end": v(51.68, 51.68) * mm, "construction": true});
            skLineSegment(sketch, "E16.0.47", {"start": v(51.68, 51.68) * mm, "end": v(50.99, 56.63) * mm, "construction": true});
            skLineSegment(sketch, "E16.0.48", {"start": v(50.99, 56.63) * mm, "end": v(46, 56.8) * mm, "construction": true});
            skLineSegment(sketch, "E16.0.49", {"start": v(46, 56.8) * mm, "end": v(44.79, 61.65) * mm, "construction": true});
            skLineSegment(sketch, "E16.0.50", {"start": v(44.79, 61.65) * mm, "end": v(39.8, 61.3) * mm, "construction": true});
            skLineSegment(sketch, "E16.0.51", {"start": v(39.8, 61.3) * mm, "end": v(38.1, 66) * mm, "construction": true});
            skLineSegment(sketch, "E16.0.52", {"start": v(38.1, 66) * mm, "end": v(33.18, 65.12) * mm, "construction": true});
            skLineSegment(sketch, "E16.0.53", {"start": v(33.18, 65.12) * mm, "end": v(31, 69.61) * mm, "construction": true});
            skLineSegment(sketch, "E16.0.54", {"start": v(31, 69.61) * mm, "end": v(26.2, 68.24) * mm, "construction": true});
            skLineSegment(sketch, "E16.0.55", {"start": v(26.2, 68.24) * mm, "end": v(23.55, 72.47) * mm, "construction": true});
            skLineSegment(sketch, "E16.0.56", {"start": v(23.55, 72.47) * mm, "end": v(18.92, 70.6) * mm, "construction": true});
            skLineSegment(sketch, "E16.0.57", {"start": v(18.92, 70.6) * mm, "end": v(15.84, 74.53) * mm, "construction": true});
            skLineSegment(sketch, "E16.0.58", {"start": v(15.84, 74.53) * mm, "end": v(11.43, 72.2) * mm, "construction": true});
            skLineSegment(sketch, "E16.0.59", {"start": v(11.43, 72.2) * mm, "end": v(7.97, 75.78) * mm, "construction": true});
            skLineSegment(sketch, "E16.0.60", {"start": v(7.97, 75.78) * mm, "end": v(3.83, 73) * mm, "construction": true});
            skLineSegment(sketch, "E16.0.61", {"start": v(3.83, 73) * mm, "end": v(0, 76.2) * mm, "construction": true});
            skLineSegment(sketch, "E16.0.62", {"start": v(0, 76.2) * mm, "end": v(-3.83, 73) * mm, "construction": true});
            skLineSegment(sketch, "E16.0.63", {"start": v(-3.83, 73) * mm, "end": v(-7.97, 75.78) * mm, "construction": true});
            skLineSegment(sketch, "E16.0.64", {"start": v(-7.97, 75.78) * mm, "end": v(-11.43, 72.2) * mm, "construction": true});
            skLineSegment(sketch, "E16.0.65", {"start": v(-11.43, 72.2) * mm, "end": v(-15.84, 74.53) * mm, "construction": true});
            skLineSegment(sketch, "E16.0.66", {"start": v(-15.84, 74.53) * mm, "end": v(-18.92, 70.6) * mm, "construction": true});
            skLineSegment(sketch, "E16.0.67", {"start": v(-18.92, 70.6) * mm, "end": v(-23.55, 72.47) * mm, "construction": true});
            skLineSegment(sketch, "E16.0.68", {"start": v(-23.55, 72.47) * mm, "end": v(-26.2, 68.24) * mm, "construction": true});
            skLineSegment(sketch, "E16.0.69", {"start": v(-26.2, 68.24) * mm, "end": v(-31, 69.61) * mm, "construction": true});
            skLineSegment(sketch, "E16.0.70", {"start": v(-31, 69.61) * mm, "end": v(-33.18, 65.12) * mm, "construction": true});
            skLineSegment(sketch, "E16.0.71", {"start": v(-33.18, 65.12) * mm, "end": v(-38.1, 66) * mm, "construction": true});
            skLineSegment(sketch, "E16.0.72", {"start": v(-38.1, 66) * mm, "end": v(-39.8, 61.3) * mm, "construction": true});
            skLineSegment(sketch, "E16.0.73", {"start": v(-39.8, 61.3) * mm, "end": v(-44.79, 61.65) * mm, "construction": true});
            skLineSegment(sketch, "E16.0.74", {"start": v(-44.79, 61.65) * mm, "end": v(-46, 56.8) * mm, "construction": true});
            skLineSegment(sketch, "E16.0.75", {"start": v(-46, 56.8) * mm, "end": v(-50.99, 56.63) * mm, "construction": true});
            skLineSegment(sketch, "E16.0.76", {"start": v(-50.99, 56.63) * mm, "end": v(-51.68, 51.68) * mm, "construction": true});
            skLineSegment(sketch, "E16.0.77", {"start": v(-51.68, 51.68) * mm, "end": v(-56.63, 50.99) * mm, "construction": true});
            skLineSegment(sketch, "E16.0.78", {"start": v(-56.63, 50.99) * mm, "end": v(-56.8, 46) * mm, "construction": true});
            skLineSegment(sketch, "E16.0.79", {"start": v(-56.8, 46) * mm, "end": v(-61.65, 44.79) * mm, "construction": true});
            skLineSegment(sketch, "E16.0.80", {"start": v(-61.65, 44.79) * mm, "end": v(-61.3, 39.8) * mm, "construction": true});
            skLineSegment(sketch, "E16.0.81", {"start": v(-61.3, 39.8) * mm, "end": v(-66, 38.1) * mm, "construction": true});
            skLineSegment(sketch, "E16.0.82", {"start": v(-66, 38.1) * mm, "end": v(-65.12, 33.18) * mm, "construction": true});
            skLineSegment(sketch, "E16.0.83", {"start": v(-65.12, 33.18) * mm, "end": v(-69.61, 31) * mm, "construction": true});
            skLineSegment(sketch, "E16.0.84", {"start": v(-69.61, 31) * mm, "end": v(-68.24, 26.2) * mm, "construction": true});
            skLineSegment(sketch, "E16.0.85", {"start": v(-68.24, 26.2) * mm, "end": v(-72.47, 23.55) * mm, "construction": true});
            skLineSegment(sketch, "E16.0.86", {"start": v(-72.47, 23.55) * mm, "end": v(-70.6, 18.92) * mm, "construction": true});
            skLineSegment(sketch, "E16.0.87", {"start": v(-70.6, 18.92) * mm, "end": v(-74.53, 15.84) * mm, "construction": true});
            skLineSegment(sketch, "E16.0.88", {"start": v(-74.53, 15.84) * mm, "end": v(-72.2, 11.43) * mm, "construction": true});
            skLineSegment(sketch, "E16.0.89", {"start": v(-72.2, 11.43) * mm, "end": v(-75.78, 7.97) * mm, "construction": true});
            skLineSegment(sketch, "E16.0.90", {"start": v(-75.78, 7.97) * mm, "end": v(-73, 3.83) * mm, "construction": true});
            skLineSegment(sketch, "E16.0.91", {"start": v(-73, 3.83) * mm, "end": v(-76.2, 0) * mm, "construction": true});
            skLineSegment(sketch, "E16.0.92", {"start": v(-76.2, 0) * mm, "end": v(-73, -3.83) * mm, "construction": true});
            skLineSegment(sketch, "E16.0.93", {"start": v(-73, -3.83) * mm, "end": v(-75.78, -7.97) * mm, "construction": true});
            skLineSegment(sketch, "E16.0.94", {"start": v(-75.78, -7.97) * mm, "end": v(-72.2, -11.43) * mm, "construction": true});
            skLineSegment(sketch, "E16.0.95", {"start": v(-72.2, -11.43) * mm, "end": v(-74.53, -15.84) * mm, "construction": true});
            skLineSegment(sketch, "E16.0.96", {"start": v(-74.53, -15.84) * mm, "end": v(-70.6, -18.92) * mm, "construction": true});
            skLineSegment(sketch, "E16.0.97", {"start": v(-70.6, -18.92) * mm, "end": v(-72.47, -23.55) * mm, "construction": true});
            skLineSegment(sketch, "E16.0.98", {"start": v(-72.47, -23.55) * mm, "end": v(-68.24, -26.2) * mm, "construction": true});
            skLineSegment(sketch, "E16.0.99", {"start": v(-68.24, -26.2) * mm, "end": v(-69.61, -31) * mm, "construction": true});
            skLineSegment(sketch, "E16.0.100", {"start": v(-69.61, -31) * mm, "end": v(-65.12, -33.18) * mm, "construction": true});
            skLineSegment(sketch, "E16.0.101", {"start": v(-65.12, -33.18) * mm, "end": v(-66, -38.1) * mm, "construction": true});
            skLineSegment(sketch, "E16.0.102", {"start": v(-66, -38.1) * mm, "end": v(-61.3, -39.8) * mm, "construction": true});
            skLineSegment(sketch, "E16.0.103", {"start": v(-61.3, -39.8) * mm, "end": v(-61.65, -44.79) * mm, "construction": true});
            skLineSegment(sketch, "E16.0.104", {"start": v(-61.65, -44.79) * mm, "end": v(-56.8, -46) * mm, "construction": true});
            skLineSegment(sketch, "E16.0.105", {"start": v(-56.8, -46) * mm, "end": v(-56.63, -50.99) * mm, "construction": true});
            skLineSegment(sketch, "E16.0.106", {"start": v(-56.63, -50.99) * mm, "end": v(-51.68, -51.68) * mm, "construction": true});
            skLineSegment(sketch, "E16.0.107", {"start": v(-51.68, -51.68) * mm, "end": v(-50.99, -56.63) * mm, "construction": true});
            skLineSegment(sketch, "E16.0.108", {"start": v(-50.99, -56.63) * mm, "end": v(-46, -56.8) * mm, "construction": true});
            skLineSegment(sketch, "E16.0.109", {"start": v(-46, -56.8) * mm, "end": v(-44.79, -61.65) * mm, "construction": true});
            skLineSegment(sketch, "E16.0.110", {"start": v(-44.79, -61.65) * mm, "end": v(-39.8, -61.3) * mm, "construction": true});
            skLineSegment(sketch, "E16.0.111", {"start": v(-39.8, -61.3) * mm, "end": v(-38.1, -66) * mm, "construction": true});
            skLineSegment(sketch, "E16.0.112", {"start": v(-38.1, -66) * mm, "end": v(-33.18, -65.12) * mm, "construction": true});
            skLineSegment(sketch, "E16.0.113", {"start": v(-33.18, -65.12) * mm, "end": v(-31, -69.61) * mm, "construction": true});
            skLineSegment(sketch, "E16.0.114", {"start": v(-31, -69.61) * mm, "end": v(-26.2, -68.24) * mm, "construction": true});
            skLineSegment(sketch, "E16.0.115", {"start": v(-26.2, -68.24) * mm, "end": v(-23.55, -72.47) * mm, "construction": true});
            skLineSegment(sketch, "E16.0.116", {"start": v(-23.55, -72.47) * mm, "end": v(-18.92, -70.6) * mm, "construction": true});
            skLineSegment(sketch, "E16.0.117", {"start": v(-18.92, -70.6) * mm, "end": v(-15.84, -74.53) * mm, "construction": true});
            skLineSegment(sketch, "E16.0.118", {"start": v(-15.84, -74.53) * mm, "end": v(-11.43, -72.2) * mm, "construction": true});
            skLineSegment(sketch, "E16.0.119", {"start": v(-11.43, -72.2) * mm, "end": v(-7.97, -75.78) * mm, "construction": true});
            skLineSegment(sketch, "E17.0", {"start": v(-50.28, -50.28) * mm, "end": v(-49.6, -55.09) * mm});
            skLineSegment(sketch, "E17.1", {"start": v(-55.09, -49.6) * mm, "end": v(-50.28, -50.28) * mm});
            skLineSegment(sketch, "E17.2", {"start": v(-55.26, -44.75) * mm, "end": v(-55.09, -49.6) * mm});
            skLineSegment(sketch, "E17.3", {"start": v(-59.97, -43.57) * mm, "end": v(-55.26, -44.75) * mm});
            skLineSegment(sketch, "E17.4", {"start": v(-59.63, -38.73) * mm, "end": v(-59.97, -43.57) * mm});
            skLineSegment(sketch, "E17.5", {"start": v(-64.2, -37.06) * mm, "end": v(-59.63, -38.73) * mm});
            skLineSegment(sketch, "E17.6", {"start": v(-63.35, -32.28) * mm, "end": v(-64.2, -37.06) * mm});
            skLineSegment(sketch, "E17.7", {"start": v(-67.72, -30.15) * mm, "end": v(-63.35, -32.28) * mm});
            skLineSegment(sketch, "E17.8", {"start": v(-66.38, -25.48) * mm, "end": v(-67.72, -30.15) * mm});
            skLineSegment(sketch, "E17.9", {"start": v(-70.5, -22.9) * mm, "end": v(-66.38, -25.48) * mm});
            skLineSegment(sketch, "E17.10", {"start": v(-68.68, -18.4) * mm, "end": v(-70.5, -22.9) * mm});
            skLineSegment(sketch, "E17.11", {"start": v(-72.5, -15.41) * mm, "end": v(-68.68, -18.4) * mm});
            skLineSegment(sketch, "E17.12", {"start": v(-70.23, -11.12) * mm, "end": v(-72.5, -15.41) * mm});
            skLineSegment(sketch, "E17.13", {"start": v(-73.72, -7.75) * mm, "end": v(-70.23, -11.12) * mm});
            skLineSegment(sketch, "E17.14", {"start": v(-71, -3.72) * mm, "end": v(-73.72, -7.75) * mm});
            skLineSegment(sketch, "E17.15", {"start": v(-74.13, 0) * mm, "end": v(-71, -3.72) * mm});
            skLineSegment(sketch, "E17.16", {"start": v(-71, 3.72) * mm, "end": v(-74.13, 0) * mm});
            skLineSegment(sketch, "E17.17", {"start": v(-73.72, 7.75) * mm, "end": v(-71, 3.72) * mm});
            skLineSegment(sketch, "E17.18", {"start": v(-70.23, 11.12) * mm, "end": v(-73.72, 7.75) * mm});
            skLineSegment(sketch, "E17.19", {"start": v(-72.5, 15.41) * mm, "end": v(-70.23, 11.12) * mm});
            skLineSegment(sketch, "E17.20", {"start": v(-68.68, 18.4) * mm, "end": v(-72.5, 15.41) * mm});
            skLineSegment(sketch, "E17.21", {"start": v(-70.5, 22.9) * mm, "end": v(-68.68, 18.4) * mm});
            skLineSegment(sketch, "E17.22", {"start": v(-66.38, 25.48) * mm, "end": v(-70.5, 22.9) * mm});
            skLineSegment(sketch, "E17.23", {"start": v(73.72, 7.75) * mm, "end": v(70.23, 11.12) * mm});
            skLineSegment(sketch, "E17.24", {"start": v(71, 3.72) * mm, "end": v(73.72, 7.75) * mm});
            skLineSegment(sketch, "E17.25", {"start": v(74.13, 0) * mm, "end": v(71, 3.72) * mm});
            skLineSegment(sketch, "E17.26", {"start": v(71, -3.72) * mm, "end": v(74.13, 0) * mm});
            skLineSegment(sketch, "E17.27", {"start": v(73.72, -7.75) * mm, "end": v(71, -3.72) * mm});
            skLineSegment(sketch, "E17.28", {"start": v(70.23, -11.12) * mm, "end": v(73.72, -7.75) * mm});
            skLineSegment(sketch, "E17.29", {"start": v(72.5, -15.41) * mm, "end": v(70.23, -11.12) * mm});
            skLineSegment(sketch, "E17.30", {"start": v(68.68, -18.4) * mm, "end": v(72.5, -15.41) * mm});
            skLineSegment(sketch, "E17.31", {"start": v(70.5, -22.9) * mm, "end": v(68.68, -18.4) * mm});
            skLineSegment(sketch, "E17.32", {"start": v(66.38, -25.48) * mm, "end": v(70.5, -22.9) * mm});
            skLineSegment(sketch, "E17.33", {"start": v(67.72, -30.15) * mm, "end": v(66.38, -25.48) * mm});
            skLineSegment(sketch, "E17.34", {"start": v(63.35, -32.28) * mm, "end": v(67.72, -30.15) * mm});
            skLineSegment(sketch, "E17.35", {"start": v(64.2, -37.06) * mm, "end": v(63.35, -32.28) * mm});
            skLineSegment(sketch, "E17.36", {"start": v(59.63, -38.73) * mm, "end": v(64.2, -37.06) * mm});
            skLineSegment(sketch, "E17.37", {"start": v(59.97, -43.57) * mm, "end": v(59.63, -38.73) * mm});
            skLineSegment(sketch, "E17.38", {"start": v(55.26, -44.75) * mm, "end": v(59.97, -43.57) * mm});
            skLineSegment(sketch, "E17.39", {"start": v(55.09, -49.6) * mm, "end": v(55.26, -44.75) * mm});
            skLineSegment(sketch, "E17.40", {"start": v(50.28, -50.28) * mm, "end": v(55.09, -49.6) * mm});
            skLineSegment(sketch, "E17.41", {"start": v(49.6, -55.09) * mm, "end": v(50.28, -50.28) * mm});
            skLineSegment(sketch, "E17.42", {"start": v(44.75, -55.26) * mm, "end": v(49.6, -55.09) * mm});
            skLineSegment(sketch, "E17.43", {"start": v(43.57, -59.97) * mm, "end": v(44.75, -55.26) * mm});
            skLineSegment(sketch, "E17.44", {"start": v(38.73, -59.63) * mm, "end": v(43.57, -59.97) * mm});
            skLineSegment(sketch, "E17.45", {"start": v(37.06, -64.2) * mm, "end": v(38.73, -59.63) * mm});
            skLineSegment(sketch, "E17.46", {"start": v(32.28, -63.35) * mm, "end": v(37.06, -64.2) * mm});
            skLineSegment(sketch, "E17.47", {"start": v(-15.41, -72.5) * mm, "end": v(-11.12, -70.23) * mm});
            skLineSegment(sketch, "E17.48", {"start": v(-18.4, -68.68) * mm, "end": v(-15.41, -72.5) * mm});
            skLineSegment(sketch, "E17.49", {"start": v(-22.9, -70.5) * mm, "end": v(-18.4, -68.68) * mm});
            skLineSegment(sketch, "E17.50", {"start": v(-25.48, -66.38) * mm, "end": v(-22.9, -70.5) * mm});
            skLineSegment(sketch, "E17.51", {"start": v(-30.15, -67.72) * mm, "end": v(-25.48, -66.38) * mm});
            skLineSegment(sketch, "E17.52", {"start": v(-32.28, -63.35) * mm, "end": v(-30.15, -67.72) * mm});
            skLineSegment(sketch, "E17.53", {"start": v(-44.75, -55.26) * mm, "end": v(-43.57, -59.97) * mm});
            skLineSegment(sketch, "E17.54", {"start": v(-43.57, -59.97) * mm, "end": v(-38.73, -59.63) * mm});
            skLineSegment(sketch, "E17.55", {"start": v(-38.73, -59.63) * mm, "end": v(-37.06, -64.2) * mm});
            skLineSegment(sketch, "E17.56", {"start": v(-37.06, -64.2) * mm, "end": v(-32.28, -63.35) * mm});
            skLineSegment(sketch, "E17.57", {"start": v(-11.12, -70.23) * mm, "end": v(-7.75, -73.72) * mm});
            skLineSegment(sketch, "E17.58", {"start": v(-7.75, -73.72) * mm, "end": v(-3.72, -71) * mm});
            skLineSegment(sketch, "E17.59", {"start": v(-3.72, -71) * mm, "end": v(0, -74.13) * mm});
            skLineSegment(sketch, "E17.60", {"start": v(0, -74.13) * mm, "end": v(3.72, -71) * mm});
            skLineSegment(sketch, "E17.61", {"start": v(3.72, -71) * mm, "end": v(7.75, -73.72) * mm});
            skLineSegment(sketch, "E17.62", {"start": v(7.75, -73.72) * mm, "end": v(11.12, -70.23) * mm});
            skLineSegment(sketch, "E17.63", {"start": v(11.12, -70.23) * mm, "end": v(15.41, -72.5) * mm});
            skLineSegment(sketch, "E17.64", {"start": v(15.41, -72.5) * mm, "end": v(18.4, -68.68) * mm});
            skLineSegment(sketch, "E17.65", {"start": v(18.4, -68.68) * mm, "end": v(22.9, -70.5) * mm});
            skLineSegment(sketch, "E17.66", {"start": v(22.9, -70.5) * mm, "end": v(25.48, -66.38) * mm});
            skLineSegment(sketch, "E17.67", {"start": v(25.48, -66.38) * mm, "end": v(30.15, -67.72) * mm});
            skLineSegment(sketch, "E17.68", {"start": v(30.15, -67.72) * mm, "end": v(32.28, -63.35) * mm});
            skLineSegment(sketch, "E17.69", {"start": v(70.23, 11.12) * mm, "end": v(72.5, 15.41) * mm});
            skLineSegment(sketch, "E17.70", {"start": v(72.5, 15.41) * mm, "end": v(68.68, 18.4) * mm});
            skLineSegment(sketch, "E17.71", {"start": v(68.68, 18.4) * mm, "end": v(70.5, 22.9) * mm});
            skLineSegment(sketch, "E17.72", {"start": v(70.5, 22.9) * mm, "end": v(66.38, 25.48) * mm});
            skLineSegment(sketch, "E17.73", {"start": v(66.38, 25.48) * mm, "end": v(67.72, 30.15) * mm});
            skLineSegment(sketch, "E17.74", {"start": v(67.72, 30.15) * mm, "end": v(63.35, 32.28) * mm});
            skLineSegment(sketch, "E17.75", {"start": v(63.35, 32.28) * mm, "end": v(64.2, 37.06) * mm});
            skLineSegment(sketch, "E17.76", {"start": v(64.2, 37.06) * mm, "end": v(59.63, 38.73) * mm});
            skLineSegment(sketch, "E17.77", {"start": v(59.63, 38.73) * mm, "end": v(59.97, 43.57) * mm});
            skLineSegment(sketch, "E17.78", {"start": v(59.97, 43.57) * mm, "end": v(55.26, 44.75) * mm});
            skLineSegment(sketch, "E17.79", {"start": v(55.26, 44.75) * mm, "end": v(55.09, 49.6) * mm});
            skLineSegment(sketch, "E17.80", {"start": v(55.09, 49.6) * mm, "end": v(50.28, 50.28) * mm});
            skLineSegment(sketch, "E17.81", {"start": v(50.28, 50.28) * mm, "end": v(49.6, 55.09) * mm});
            skLineSegment(sketch, "E17.82", {"start": v(49.6, 55.09) * mm, "end": v(44.75, 55.26) * mm});
            skLineSegment(sketch, "E17.83", {"start": v(44.75, 55.26) * mm, "end": v(43.57, 59.97) * mm});
            skLineSegment(sketch, "E17.84", {"start": v(43.57, 59.97) * mm, "end": v(38.73, 59.63) * mm});
            skLineSegment(sketch, "E17.85", {"start": v(38.73, 59.63) * mm, "end": v(37.06, 64.2) * mm});
            skLineSegment(sketch, "E17.86", {"start": v(37.06, 64.2) * mm, "end": v(32.28, 63.35) * mm});
            skLineSegment(sketch, "E17.87", {"start": v(32.28, 63.35) * mm, "end": v(30.15, 67.72) * mm});
            skLineSegment(sketch, "E17.88", {"start": v(30.15, 67.72) * mm, "end": v(25.48, 66.38) * mm});
            skLineSegment(sketch, "E17.89", {"start": v(25.48, 66.38) * mm, "end": v(22.9, 70.5) * mm});
            skLineSegment(sketch, "E17.90", {"start": v(22.9, 70.5) * mm, "end": v(18.4, 68.68) * mm});
            skLineSegment(sketch, "E17.91", {"start": v(18.4, 68.68) * mm, "end": v(15.41, 72.5) * mm});
            skLineSegment(sketch, "E17.92", {"start": v(-49.6, -55.09) * mm, "end": v(-44.75, -55.26) * mm});
            skLineSegment(sketch, "E17.93", {"start": v(15.41, 72.5) * mm, "end": v(11.12, 70.23) * mm});
            skLineSegment(sketch, "E17.94", {"start": v(11.12, 70.23) * mm, "end": v(7.75, 73.72) * mm});
            skLineSegment(sketch, "E17.95", {"start": v(7.75, 73.72) * mm, "end": v(3.72, 71) * mm});
            skLineSegment(sketch, "E17.96", {"start": v(3.72, 71) * mm, "end": v(0, 74.13) * mm});
            skLineSegment(sketch, "E17.97", {"start": v(0, 74.13) * mm, "end": v(-3.72, 71) * mm});
            skLineSegment(sketch, "E17.98", {"start": v(-3.72, 71) * mm, "end": v(-7.75, 73.72) * mm});
            skLineSegment(sketch, "E17.99", {"start": v(-7.75, 73.72) * mm, "end": v(-11.12, 70.23) * mm});
            skLineSegment(sketch, "E17.100", {"start": v(-11.12, 70.23) * mm, "end": v(-15.41, 72.5) * mm});
            skLineSegment(sketch, "E17.101", {"start": v(-15.41, 72.5) * mm, "end": v(-18.4, 68.68) * mm});
            skLineSegment(sketch, "E17.102", {"start": v(-18.4, 68.68) * mm, "end": v(-22.9, 70.5) * mm});
            skLineSegment(sketch, "E17.103", {"start": v(-22.9, 70.5) * mm, "end": v(-25.48, 66.38) * mm});
            skLineSegment(sketch, "E17.104", {"start": v(-25.48, 66.38) * mm, "end": v(-30.15, 67.72) * mm});
            skLineSegment(sketch, "E17.105", {"start": v(-30.15, 67.72) * mm, "end": v(-32.28, 63.35) * mm});
            skLineSegment(sketch, "E17.106", {"start": v(-32.28, 63.35) * mm, "end": v(-37.06, 64.2) * mm});
            skLineSegment(sketch, "E17.107", {"start": v(-37.06, 64.2) * mm, "end": v(-38.73, 59.63) * mm});
            skLineSegment(sketch, "E17.108", {"start": v(-38.73, 59.63) * mm, "end": v(-43.57, 59.97) * mm});
            skLineSegment(sketch, "E17.109", {"start": v(-43.57, 59.97) * mm, "end": v(-44.75, 55.26) * mm});
            skLineSegment(sketch, "E17.110", {"start": v(-44.75, 55.26) * mm, "end": v(-49.6, 55.09) * mm});
            skLineSegment(sketch, "E17.111", {"start": v(-49.6, 55.09) * mm, "end": v(-50.28, 50.28) * mm});
            skLineSegment(sketch, "E17.112", {"start": v(-50.28, 50.28) * mm, "end": v(-55.09, 49.6) * mm});
            skLineSegment(sketch, "E17.113", {"start": v(-55.09, 49.6) * mm, "end": v(-55.26, 44.75) * mm});
            skLineSegment(sketch, "E17.114", {"start": v(-55.26, 44.75) * mm, "end": v(-59.97, 43.57) * mm});
            skLineSegment(sketch, "E17.115", {"start": v(-59.97, 43.57) * mm, "end": v(-59.63, 38.73) * mm});
            skLineSegment(sketch, "E17.116", {"start": v(-59.63, 38.73) * mm, "end": v(-64.2, 37.06) * mm});
            skLineSegment(sketch, "E17.117", {"start": v(-64.2, 37.06) * mm, "end": v(-63.35, 32.28) * mm});
            skLineSegment(sketch, "E17.118", {"start": v(-63.35, 32.28) * mm, "end": v(-67.72, 30.15) * mm});
            skLineSegment(sketch, "E17.119", {"start": v(-67.72, 30.15) * mm, "end": v(-66.38, 25.48) * mm});
            skSolve(sketch);
        }
        {
            var Q1;
            Q1=makeQuery(id+"F7.imprint","IMPRINT",FACE,{"disambiguationData":[TD([[makeQuery(id+"F7.imprint","IMPRINT",EDGE,{"derivedFrom":sQuery(id+"F7.wireOp",EDGE,"E15.0")}),1.0]])]});
            var Q2;
            Q2 = qSketchRegion(id + "F8", true);
            loft(context, id + "F9", {"operationType" : NewBodyOperationType.REMOVE, "sheetProfilesArray" : [{ "sheetProfileEntities" : qUnion([Q1]) }, { "sheetProfileEntities" : qUnion([Q2]) }]});
        }
        {
            var Q0;
            Q0=makeQuery(id+"F6.boolean.opBoolean","COPY",FACE,{"derivedFrom":makeQuery(id+"F6.opExtrude","CAP_FACE",FACE,{"disambiguationData":[OSD([sQuery(id+"F5.wireOp",EDGE,"E14.bottom"),sQuery(id+"F5.wireOp",EDGE,"E14.top"),sQuery(id+"F5.wireOp",EDGE,"E14.left"),sQuery(id+"F5.wireOp",EDGE,"E14.right")])],"isStart":true})});
            var sketch = newSketch(context, id + "F10", { "sketchPlane" : qUnion([Q0])});
            skLineSegment(sketch, "E18.0", {"start": v(-7.25, 45.76) * mm, "end": v(-10.04, 47.24) * mm});
            skLineSegment(sketch, "E18.1", {"start": v(-10.04, 47.24) * mm, "end": v(-12, 44.75) * mm});
            skLineSegment(sketch, "E18.2", {"start": v(-12, 44.75) * mm, "end": v(-14.93, 45.94) * mm});
            skLineSegment(sketch, "E18.3", {"start": v(-14.93, 45.94) * mm, "end": v(-16.6, 43.25) * mm});
            skLineSegment(sketch, "E18.4", {"start": v(-16.6, 43.25) * mm, "end": v(-19.65, 44.12) * mm});
            skLineSegment(sketch, "E18.5", {"start": v(-19.65, 44.12) * mm, "end": v(-21.03, 41.28) * mm});
            skLineSegment(sketch, "E18.6", {"start": v(-21.03, 41.28) * mm, "end": v(-24.15, 41.83) * mm});
            skLineSegment(sketch, "E18.7", {"start": v(-24.15, 41.83) * mm, "end": v(-25.23, 38.85) * mm});
            skLineSegment(sketch, "E18.8", {"start": v(-25.23, 38.85) * mm, "end": v(-28.39, 39.08) * mm});
            skLineSegment(sketch, "E18.9", {"start": v(-28.39, 39.08) * mm, "end": v(-29.16, 36) * mm});
            skLineSegment(sketch, "E18.10", {"start": v(-29.16, 36) * mm, "end": v(-32.32, 35.9) * mm});
            skLineSegment(sketch, "E18.11", {"start": v(-32.32, 35.9) * mm, "end": v(-32.76, 32.76) * mm});
            skLineSegment(sketch, "E18.12", {"start": v(-32.76, 32.76) * mm, "end": v(-35.9, 32.32) * mm});
            skLineSegment(sketch, "E18.13", {"start": v(-35.9, 32.32) * mm, "end": v(-36, 29.16) * mm});
            skLineSegment(sketch, "E18.14", {"start": v(-36, 29.16) * mm, "end": v(-39.08, 28.39) * mm});
            skLineSegment(sketch, "E18.15", {"start": v(-5.05, 48.04) * mm, "end": v(-7.25, 45.76) * mm});
            skLineSegment(sketch, "E18.16", {"start": v(-2.42, 46.27) * mm, "end": v(-5.05, 48.04) * mm});
            skLineSegment(sketch, "E18.17", {"start": v(0, 48.3) * mm, "end": v(-2.42, 46.27) * mm});
            skLineSegment(sketch, "E18.18", {"start": v(2.42, 46.27) * mm, "end": v(0, 48.3) * mm});
            skLineSegment(sketch, "E18.19", {"start": v(5.05, 48.04) * mm, "end": v(2.42, 46.27) * mm});
            skLineSegment(sketch, "E18.20", {"start": v(7.25, 45.76) * mm, "end": v(5.05, 48.04) * mm});
            skLineSegment(sketch, "E18.21", {"start": v(10.04, 47.24) * mm, "end": v(7.25, 45.76) * mm});
            skLineSegment(sketch, "E18.22", {"start": v(12, 44.75) * mm, "end": v(10.04, 47.24) * mm});
            skLineSegment(sketch, "E18.23", {"start": v(14.93, 45.94) * mm, "end": v(12, 44.75) * mm});
            skLineSegment(sketch, "E18.24", {"start": v(16.6, 43.25) * mm, "end": v(14.93, 45.94) * mm});
            skLineSegment(sketch, "E18.25", {"start": v(19.65, 44.12) * mm, "end": v(16.6, 43.25) * mm});
            skLineSegment(sketch, "E18.26", {"start": v(-39.08, 28.39) * mm, "end": v(-38.85, 25.23) * mm});
            skLineSegment(sketch, "E18.27", {"start": v(-38.85, 25.23) * mm, "end": v(-41.83, 24.15) * mm});
            skLineSegment(sketch, "E18.28", {"start": v(-41.83, 24.15) * mm, "end": v(-41.28, 21.03) * mm});
            skLineSegment(sketch, "E18.29", {"start": v(-41.28, 21.03) * mm, "end": v(-44.12, 19.65) * mm});
            skLineSegment(sketch, "E18.30", {"start": v(-44.12, 19.65) * mm, "end": v(-43.25, 16.6) * mm});
            skLineSegment(sketch, "E18.31", {"start": v(-43.25, 16.6) * mm, "end": v(-45.94, 14.93) * mm});
            skLineSegment(sketch, "E18.32", {"start": v(-45.94, 14.93) * mm, "end": v(-44.75, 12) * mm});
            skLineSegment(sketch, "E18.33", {"start": v(-44.75, 12) * mm, "end": v(-47.24, 10.04) * mm});
            skLineSegment(sketch, "E18.34", {"start": v(-47.24, 10.04) * mm, "end": v(-45.76, 7.25) * mm});
            skLineSegment(sketch, "E18.35", {"start": v(-45.76, 7.25) * mm, "end": v(-48.04, 5.05) * mm});
            skLineSegment(sketch, "E18.36", {"start": v(-48.04, 5.05) * mm, "end": v(-46.27, 2.42) * mm});
            skLineSegment(sketch, "E18.37", {"start": v(-46.27, 2.42) * mm, "end": v(-48.3, 0) * mm});
            skLineSegment(sketch, "E18.38", {"start": v(-48.3, 0) * mm, "end": v(-46.27, -2.42) * mm});
            skLineSegment(sketch, "E18.39", {"start": v(-46.27, -2.42) * mm, "end": v(-48.04, -5.05) * mm});
            skLineSegment(sketch, "E18.40", {"start": v(-48.04, -5.05) * mm, "end": v(-45.76, -7.25) * mm});
            skLineSegment(sketch, "E18.41", {"start": v(-45.76, -7.25) * mm, "end": v(-47.24, -10.04) * mm});
            skLineSegment(sketch, "E18.42", {"start": v(-47.24, -10.04) * mm, "end": v(-44.75, -12) * mm});
            skLineSegment(sketch, "E18.43", {"start": v(-44.75, -12) * mm, "end": v(-45.94, -14.93) * mm});
            skLineSegment(sketch, "E18.44", {"start": v(-45.94, -14.93) * mm, "end": v(-43.25, -16.6) * mm});
            skLineSegment(sketch, "E18.45", {"start": v(-43.25, -16.6) * mm, "end": v(-44.12, -19.65) * mm});
            skLineSegment(sketch, "E18.46", {"start": v(-44.12, -19.65) * mm, "end": v(-41.28, -21.03) * mm});
            skLineSegment(sketch, "E18.47", {"start": v(-41.28, -21.03) * mm, "end": v(-41.83, -24.15) * mm});
            skLineSegment(sketch, "E18.48", {"start": v(-41.83, -24.15) * mm, "end": v(-38.85, -25.23) * mm});
            skLineSegment(sketch, "E18.49", {"start": v(-38.85, -25.23) * mm, "end": v(-39.08, -28.39) * mm});
            skLineSegment(sketch, "E18.50", {"start": v(-39.08, -28.39) * mm, "end": v(-36, -29.16) * mm});
            skLineSegment(sketch, "E18.51", {"start": v(-36, -29.16) * mm, "end": v(-35.9, -32.32) * mm});
            skLineSegment(sketch, "E18.52", {"start": v(-35.9, -32.32) * mm, "end": v(-32.76, -32.76) * mm});
            skLineSegment(sketch, "E18.53", {"start": v(-32.76, -32.76) * mm, "end": v(-32.32, -35.9) * mm});
            skLineSegment(sketch, "E18.54", {"start": v(-32.32, -35.9) * mm, "end": v(-29.16, -36) * mm});
            skLineSegment(sketch, "E18.55", {"start": v(-29.16, -36) * mm, "end": v(-28.39, -39.08) * mm});
            skLineSegment(sketch, "E18.56", {"start": v(-28.39, -39.08) * mm, "end": v(-25.23, -38.85) * mm});
            skLineSegment(sketch, "E18.57", {"start": v(-25.23, -38.85) * mm, "end": v(-24.15, -41.83) * mm});
            skLineSegment(sketch, "E18.58", {"start": v(-24.15, -41.83) * mm, "end": v(-21.03, -41.28) * mm});
            skLineSegment(sketch, "E18.59", {"start": v(-21.03, -41.28) * mm, "end": v(-19.65, -44.12) * mm});
            skLineSegment(sketch, "E18.60", {"start": v(-19.65, -44.12) * mm, "end": v(-16.6, -43.25) * mm});
            skLineSegment(sketch, "E18.61", {"start": v(-16.6, -43.25) * mm, "end": v(-14.93, -45.94) * mm});
            skLineSegment(sketch, "E18.62", {"start": v(-14.93, -45.94) * mm, "end": v(-12, -44.75) * mm});
            skLineSegment(sketch, "E18.63", {"start": v(-12, -44.75) * mm, "end": v(-10.04, -47.24) * mm});
            skLineSegment(sketch, "E18.64", {"start": v(-10.04, -47.24) * mm, "end": v(-7.25, -45.76) * mm});
            skLineSegment(sketch, "E18.65", {"start": v(-7.25, -45.76) * mm, "end": v(-5.05, -48.04) * mm});
            skLineSegment(sketch, "E18.66", {"start": v(-5.05, -48.04) * mm, "end": v(-2.42, -46.27) * mm});
            skLineSegment(sketch, "E18.67", {"start": v(-2.42, -46.27) * mm, "end": v(0, -48.3) * mm});
            skLineSegment(sketch, "E18.68", {"start": v(0, -48.3) * mm, "end": v(2.42, -46.27) * mm});
            skLineSegment(sketch, "E18.69", {"start": v(2.42, -46.27) * mm, "end": v(5.05, -48.04) * mm});
            skLineSegment(sketch, "E18.70", {"start": v(5.05, -48.04) * mm, "end": v(7.25, -45.76) * mm});
            skLineSegment(sketch, "E18.71", {"start": v(7.25, -45.76) * mm, "end": v(10.04, -47.24) * mm});
            skLineSegment(sketch, "E18.72", {"start": v(10.04, -47.24) * mm, "end": v(12, -44.75) * mm});
            skLineSegment(sketch, "E18.73", {"start": v(12, -44.75) * mm, "end": v(14.93, -45.94) * mm});
            skLineSegment(sketch, "E18.74", {"start": v(14.93, -45.94) * mm, "end": v(16.6, -43.25) * mm});
            skLineSegment(sketch, "E18.75", {"start": v(16.6, -43.25) * mm, "end": v(19.65, -44.12) * mm});
            skLineSegment(sketch, "E18.76", {"start": v(19.65, -44.12) * mm, "end": v(21.03, -41.28) * mm});
            skLineSegment(sketch, "E18.77", {"start": v(21.03, -41.28) * mm, "end": v(24.15, -41.83) * mm});
            skLineSegment(sketch, "E18.78", {"start": v(24.15, -41.83) * mm, "end": v(25.23, -38.85) * mm});
            skLineSegment(sketch, "E18.79", {"start": v(25.23, -38.85) * mm, "end": v(28.39, -39.08) * mm});
            skLineSegment(sketch, "E18.80", {"start": v(28.39, -39.08) * mm, "end": v(29.16, -36) * mm});
            skLineSegment(sketch, "E18.81", {"start": v(29.16, -36) * mm, "end": v(32.32, -35.9) * mm});
            skLineSegment(sketch, "E18.82", {"start": v(32.32, -35.9) * mm, "end": v(32.76, -32.76) * mm});
            skLineSegment(sketch, "E18.83", {"start": v(32.76, -32.76) * mm, "end": v(35.9, -32.32) * mm});
            skLineSegment(sketch, "E18.84", {"start": v(35.9, -32.32) * mm, "end": v(36, -29.16) * mm});
            skLineSegment(sketch, "E18.85", {"start": v(36, -29.16) * mm, "end": v(39.08, -28.39) * mm});
            skLineSegment(sketch, "E18.86", {"start": v(39.08, -28.39) * mm, "end": v(38.85, -25.23) * mm});
            skLineSegment(sketch, "E18.87", {"start": v(38.85, -25.23) * mm, "end": v(41.83, -24.15) * mm});
            skLineSegment(sketch, "E18.88", {"start": v(41.83, -24.15) * mm, "end": v(41.28, -21.03) * mm});
            skLineSegment(sketch, "E18.89", {"start": v(41.28, -21.03) * mm, "end": v(44.12, -19.65) * mm});
            skLineSegment(sketch, "E18.90", {"start": v(44.12, -19.65) * mm, "end": v(43.25, -16.6) * mm});
            skLineSegment(sketch, "E18.91", {"start": v(43.25, -16.6) * mm, "end": v(45.94, -14.93) * mm});
            skLineSegment(sketch, "E18.92", {"start": v(45.94, -14.93) * mm, "end": v(44.75, -12) * mm});
            skLineSegment(sketch, "E18.93", {"start": v(44.75, -12) * mm, "end": v(47.24, -10.04) * mm});
            skLineSegment(sketch, "E18.94", {"start": v(47.24, -10.04) * mm, "end": v(45.76, -7.25) * mm});
            skLineSegment(sketch, "E18.95", {"start": v(45.76, -7.25) * mm, "end": v(48.04, -5.05) * mm});
            skLineSegment(sketch, "E18.96", {"start": v(48.04, -5.05) * mm, "end": v(46.27, -2.42) * mm});
            skLineSegment(sketch, "E18.97", {"start": v(21.03, 41.28) * mm, "end": v(19.65, 44.12) * mm});
            skLineSegment(sketch, "E18.98", {"start": v(24.15, 41.83) * mm, "end": v(21.03, 41.28) * mm});
            skLineSegment(sketch, "E18.99", {"start": v(25.23, 38.85) * mm, "end": v(24.15, 41.83) * mm});
            skLineSegment(sketch, "E18.100", {"start": v(28.39, 39.08) * mm, "end": v(25.23, 38.85) * mm});
            skLineSegment(sketch, "E18.101", {"start": v(29.16, 36) * mm, "end": v(28.39, 39.08) * mm});
            skLineSegment(sketch, "E18.102", {"start": v(32.32, 35.9) * mm, "end": v(29.16, 36) * mm});
            skLineSegment(sketch, "E18.103", {"start": v(32.76, 32.76) * mm, "end": v(32.32, 35.9) * mm});
            skLineSegment(sketch, "E18.104", {"start": v(35.9, 32.32) * mm, "end": v(32.76, 32.76) * mm});
            skLineSegment(sketch, "E18.105", {"start": v(36, 29.16) * mm, "end": v(35.9, 32.32) * mm});
            skLineSegment(sketch, "E18.106", {"start": v(39.08, 28.39) * mm, "end": v(36, 29.16) * mm});
            skLineSegment(sketch, "E18.107", {"start": v(38.85, 25.23) * mm, "end": v(39.08, 28.39) * mm});
            skLineSegment(sketch, "E18.108", {"start": v(41.83, 24.15) * mm, "end": v(38.85, 25.23) * mm});
            skLineSegment(sketch, "E18.109", {"start": v(41.28, 21.03) * mm, "end": v(41.83, 24.15) * mm});
            skLineSegment(sketch, "E18.110", {"start": v(44.12, 19.65) * mm, "end": v(41.28, 21.03) * mm});
            skLineSegment(sketch, "E18.111", {"start": v(43.25, 16.6) * mm, "end": v(44.12, 19.65) * mm});
            skLineSegment(sketch, "E18.112", {"start": v(45.94, 14.93) * mm, "end": v(43.25, 16.6) * mm});
            skLineSegment(sketch, "E18.113", {"start": v(44.75, 12) * mm, "end": v(45.94, 14.93) * mm});
            skLineSegment(sketch, "E18.114", {"start": v(47.24, 10.04) * mm, "end": v(44.75, 12) * mm});
            skLineSegment(sketch, "E18.115", {"start": v(45.76, 7.25) * mm, "end": v(47.24, 10.04) * mm});
            skLineSegment(sketch, "E18.116", {"start": v(48.04, 5.05) * mm, "end": v(45.76, 7.25) * mm});
            skLineSegment(sketch, "E18.117", {"start": v(46.27, 2.42) * mm, "end": v(48.04, 5.05) * mm});
            skLineSegment(sketch, "E18.118", {"start": v(48.3, 0) * mm, "end": v(46.27, 2.42) * mm});
            skLineSegment(sketch, "E18.119", {"start": v(46.27, -2.42) * mm, "end": v(48.3, 0) * mm});
            skSolve(sketch);
        }
        {
            var Q0;
            Q0 = qSketchRegion(id + "F10", true);
            extrude(context, id + "F11", {"entities" : qUnion([Q0]), "operationType" : NewBodyOperationType.ADD, "depth" : 0.8 * mm, "offsetDistance" : 25.4 * mm, "hasDraft" : true, "draftAngle" : 16 * degree, "draftPullDirection" : true});
        }
        {
            var Q0;
            Q0=qCreatedBy(id+"F4.planeOp",FACE);
            cPlane(context, id + "F12", {"entities" : qUnion([Q0]), "cplaneType" : CPlaneType.OFFSET, "offset" : 50.8 * mm, "width" : 152.4 * mm, "height" : 152.4 * mm});
        }
    });
